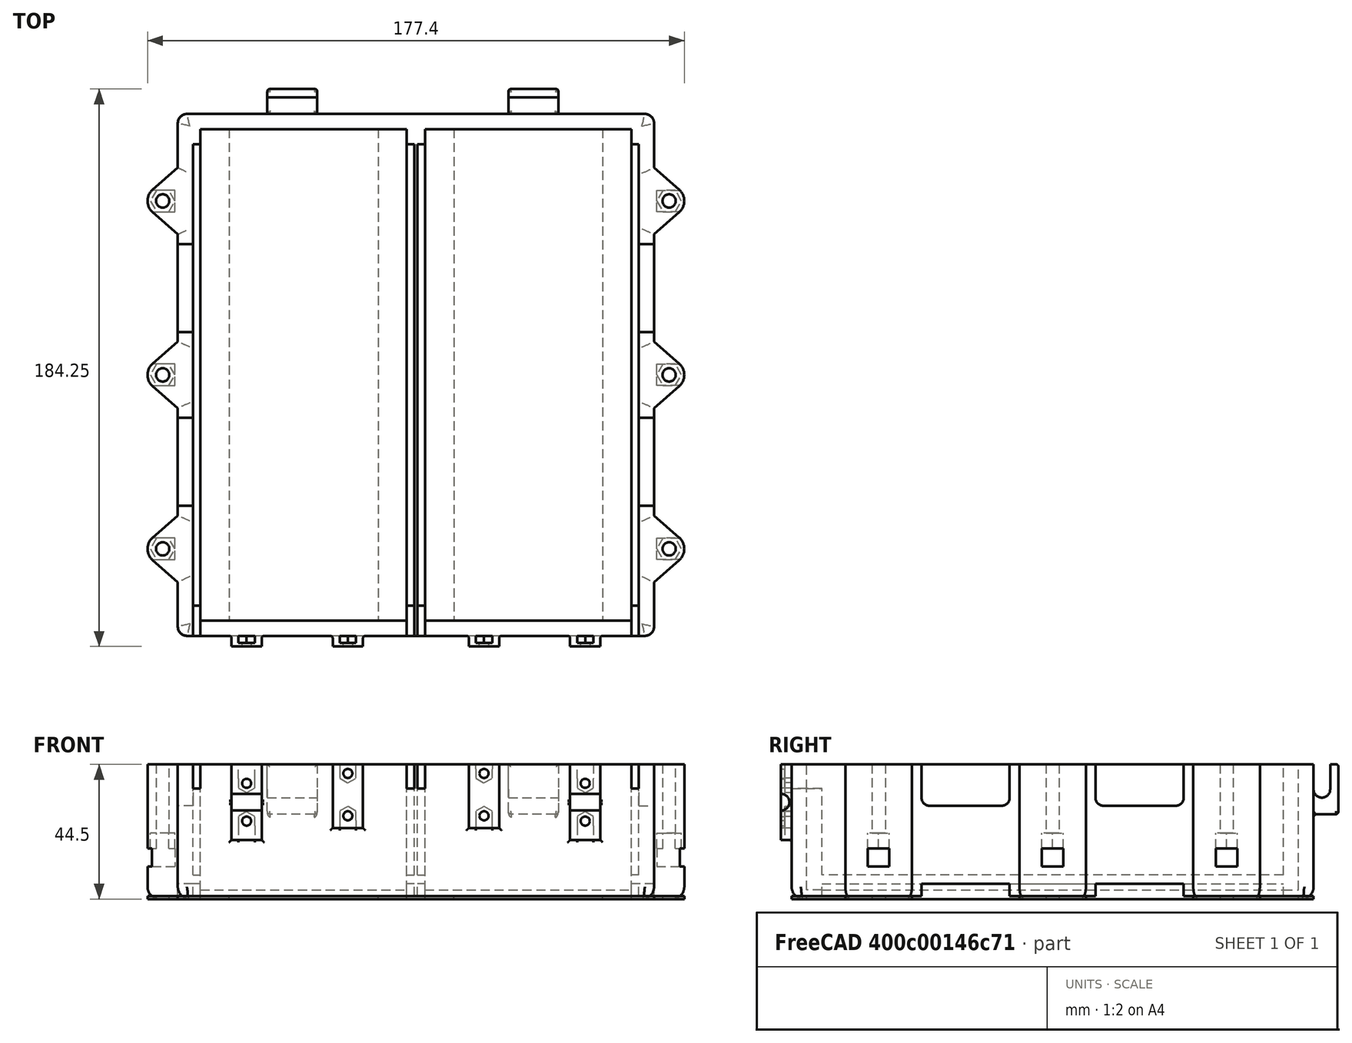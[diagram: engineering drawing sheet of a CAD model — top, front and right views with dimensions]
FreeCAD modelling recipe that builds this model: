
FCSTD DOCUMENT  (FreeCAD 0.19R24291 (Git))
Label: eskate-battery
License: All rights reserved
LicenseURL: http://en.wikipedia.org/wiki/All_rights_reserved
objects: Sketcher::SketchObject×20, PartDesign::Pocket×13, PartDesign::Plane×10, PartDesign::Fillet×10, PartDesign::Pad×7, TechDraw::DrawViewDimension×3, Spreadsheet::Sheet×2, PartDesign::Body×2, TechDraw::DrawViewPart×2, TechDraw::DrawSVGTemplate×1, PartDesign::ShapeBinder×1, TechDraw::DrawPage×1
note: 93 computed .brp shape members not serialized (recipe doc carries the construction recipe); baked Part::Feature solids carry a one-line shape summary decoded from their .brp

FEATURE [Spreadsheet::Sheet] Spreadsheet  label="measurements"
  cells = A1=batteryWidth; B1(batteryWidth)==67.2mm + batteryTolerance; D1=tolerance:; E1(batteryTolerance)==1mm; G1=cableSupportLength; H1(cableSupportLength)==25mm; J1=balanceLeadSlotHeight; K1(balanceLeadSlotHeight)==8mm; A2=batteryHeight; B2(batteryHeight)==40.5mm; G2=cableSupportWidth; H2(cableSupportWidth)=10; A3=batteryLength; B3(batteryLength)==161.5mm + batteryTolerance; D3=todo: add tolerance - but breaks sketch; G3=cableSupportHeight; H3(cableSupportHeight)==3.5mm; I3=cable to fit in 5.5mm radius; G4=cableCompressedRadius; H4(cableCompressedRadius)=2.75; A5=verticalWallThickness; B5(verticalWallThickness)==5mm; G5=m3NutAcrossFlats; H5(m3NutAcrossFlats)=5.4; A6=horizontalWallThickness; B6(horizontalWallThickness)==3mm; G6=m3NutHight; H6(m3NutHight)=2.3; A7=separatorWallThickness; B7(separatorWallThickness)==1mm; G7=m3ScrewHoleRadius; H7(m3ScrewHoleRadius)=1.5; A8=insulatorWallThickness; B8(insulatorWallThickness)==1mm; A10=nickleClearance; B10(nickleClearance)==2.5mm; A11=spacerOverlap; B11(spacerOverlap)==5mm; A13=mountingBumpRadius; B13(mountingBumpRadius)==5mm; A14=boltHoleRadius; B14(boltHoleRadius)=2.2; A15=mountingBumpTangentLength; B15(mountingBumpTangentLength)==11mm; A17=cableRadius; B17(cableRadius)==2.54mm; D17=cableRadiusLarger; E17(cableRadiusLarger)==2.75mm; A18=cableSlotWidth; B18(cableSlotWidth)==24mm; A19=balanceCableRadius; B19(balanceCableRadius)==1.25mm; A21=nutWidth; B21(nutWidth)=7.1; A22=nutHeight; B22(nutHeight)==6mm; A23=nutInsetDepth; B23(nutInsetDepth)==5mm; A25=baseFilletRadius; B25(baseFilletRadius)==4mm; A26=wallFilletRadius; B26(wallFilletRadius)==3mm; A28=spacerHeight; B28(spacerHeight)==9mm; D28=spacerTolerance; E28(spacerTolerance)==0.5mm; A29=spacerKnobbleHeight; B29(spacerKnobbleHeight)==1.6mm; C29=unused; A30=coverThickness; B30(coverThickness)==1mm
FEATURE [Sketcher::SketchObject] Sketch  label="container_shape"
  FullyConstrained = true
  MapMode = 5
  Support = -> [XY_Plane]
  expr: Constraints[23] = .Constraints.boxLength / 3
  expr: Constraints[22] = .Constraints.batteryBoxWidth / 2 + Spreadsheet.mountingBumpRadius
  expr: Constraints[65] = Spreadsheet.mountingBumpTangentLength
  expr: Constraints[19] = .Constraints.batteryBoxWidth / 2 + Spreadsheet.mountingBumpRadius
  expr: Constraints[18] = Spreadsheet.mountingBumpRadius
  expr: .Constraints.boxLength = Spreadsheet.batteryLength + 2 * Spreadsheet.verticalWallThickness
  expr: .Constraints.batteryBoxWidth = 2 * Spreadsheet.batteryWidth + 4 * Spreadsheet.nickleClearance + Spreadsheet.separatorWallThickness + 2 * Spreadsheet.verticalWallThickness
  sketch-geometry (36):
    g0: LineSegment StartX=-78.7 StartY=86.25 StartZ=0 EndX=78.7 EndY=86.25 EndZ=0
    g1: LineSegment StartX=78.7 StartY=86.25 StartZ=0 EndX=78.7 EndY=-86.25 EndZ=0
    g2: LineSegment StartX=78.7 StartY=-86.25 StartZ=0 EndX=-78.7 EndY=-86.25 EndZ=0
    g3: LineSegment StartX=-78.7 StartY=-86.25 StartZ=0 EndX=-78.7 EndY=86.25 EndZ=0
    g4: Circle CenterX=-83.7 CenterY=57.5 CenterZ=0 NormalX=0 NormalY=0 NormalZ=1 AngleXU=0 Radius=5
    g5: Circle CenterX=-83.7 CenterY=0 CenterZ=0 NormalX=0 NormalY=0 NormalZ=1 AngleXU=0 Radius=5
    g6: Circle CenterX=-83.7 CenterY=-57.5 CenterZ=0 NormalX=0 NormalY=0 NormalZ=1 AngleXU=0 Radius=5
    g7: Circle CenterX=83.7 CenterY=-57.5 CenterZ=0 NormalX=0 NormalY=0 NormalZ=1 AngleXU=0 Radius=5
    g8: Circle CenterX=83.7 CenterY=0 CenterZ=0 NormalX=0 NormalY=0 NormalZ=1 AngleXU=0 Radius=5
    g9: Circle CenterX=83.7 CenterY=57.5 CenterZ=0 NormalX=0 NormalY=0 NormalZ=1 AngleXU=0 Radius=5
    g10: LineSegment StartX=86.9877 StartY=61.2671 StartZ=0 EndX=78.7 EndY=68.5 EndZ=0
    g11: LineSegment StartX=86.9877 StartY=53.7329 StartZ=0 EndX=78.7 EndY=46.5 EndZ=0
    g12: LineSegment StartX=86.9877 StartY=3.76712 StartZ=0 EndX=78.7 EndY=11 EndZ=0
    g13: LineSegment StartX=86.9877 StartY=-3.76712 StartZ=0 EndX=78.7 EndY=-11 EndZ=0
    g14: LineSegment StartX=86.9877 StartY=-53.7329 StartZ=0 EndX=78.7 EndY=-46.5 EndZ=0
    g15: LineSegment StartX=86.9877 StartY=-61.2671 StartZ=0 EndX=78.7 EndY=-68.5 EndZ=0
    g16: LineSegment StartX=-86.9877 StartY=-61.2671 StartZ=0 EndX=-78.7 EndY=-68.5 EndZ=0
    g17: LineSegment StartX=-86.9877 StartY=-53.7329 StartZ=0 EndX=-78.7 EndY=-46.5 EndZ=0
    g18: LineSegment StartX=-86.9877 StartY=-3.76713 StartZ=0 EndX=-78.7 EndY=-11 EndZ=0
    g19: LineSegment StartX=-86.9877 StartY=3.76713 StartZ=0 EndX=-78.7 EndY=11 EndZ=0
    g20: LineSegment StartX=-86.9877 StartY=53.7329 StartZ=0 EndX=-78.7 EndY=46.5 EndZ=0
    g21: LineSegment StartX=-86.9877 StartY=61.2671 StartZ=0 EndX=-78.7 EndY=68.5 EndZ=0
    g22: ArcOfCircle CenterX=-83.7 CenterY=57.5 CenterZ=0 NormalX=0 NormalY=0 NormalZ=1 AngleXU=0 Radius=5 StartAngle=2.28834 EndAngle=3.99485
    g23: ArcOfCircle CenterX=-83.7 CenterY=0 CenterZ=0 NormalX=0 NormalY=0 NormalZ=1 AngleXU=0 Radius=5 StartAngle=2.28834 EndAngle=3.99485
    g24: ArcOfCircle CenterX=-83.7 CenterY=-57.5 CenterZ=0 NormalX=0 NormalY=0 NormalZ=1 AngleXU=0 Radius=5 StartAngle=2.28834 EndAngle=3.99485
    g25: ArcOfCircle CenterX=83.7 CenterY=-57.5 CenterZ=0 NormalX=0 NormalY=0 NormalZ=1 AngleXU=0 Radius=5 StartAngle=5.42993 EndAngle=7.13644
    g26: ArcOfCircle CenterX=83.7 CenterY=0 CenterZ=0 NormalX=0 NormalY=0 NormalZ=1 AngleXU=0 Radius=5 StartAngle=5.42993 EndAngle=7.13644
    g27: ArcOfCircle CenterX=83.7 CenterY=57.5 CenterZ=0 NormalX=0 NormalY=0 NormalZ=1 AngleXU=0 Radius=5 StartAngle=5.42993 EndAngle=7.13644
    g28: LineSegment StartX=78.7 StartY=86.25 StartZ=0 EndX=78.7 EndY=68.5 EndZ=0
    g29: LineSegment StartX=78.7 StartY=46.5 StartZ=0 EndX=78.7 EndY=11 EndZ=0
    g30: LineSegment StartX=78.7 StartY=-11 StartZ=0 EndX=78.7 EndY=-46.5 EndZ=0
    g31: LineSegment StartX=78.7 StartY=-68.5 StartZ=0 EndX=78.7 EndY=-86.25 EndZ=0
    g32: LineSegment StartX=-78.7 StartY=-86.25 StartZ=0 EndX=-78.7 EndY=-68.5 EndZ=0
    g33: LineSegment StartX=-78.7 StartY=-46.5 StartZ=0 EndX=-78.7 EndY=-11 EndZ=0
    g34: LineSegment StartX=-78.7 StartY=11 StartZ=0 EndX=-78.7 EndY=46.5 EndZ=0
    g35: LineSegment StartX=-78.7 StartY=68.5 StartZ=0 EndX=-78.7 EndY=86.25 EndZ=0
  constraints (100):
    c: Coincident(g0,g1)
    c: Coincident(g1,g2)
    c: Coincident(g2,g3)
    c: Coincident(g3,g0)
    c: Horizontal(g2)
    c: Vertical(g1)
    c: Symmetric(g0,g2,g-1)
    c: Symmetric(g0,g0,g-2)
    c: DistanceY(g3,g3) = 172.5  'boxLength'
    c: DistanceX(g0,g0) = 157.4  'batteryBoxWidth'
    c: Symmetric(g8,g5,g-2)
    c: Symmetric(g4,g9,g-2)
    c: Symmetric(g6,g7,g-2)
    c: Equal(g4,g9)
    c: Equal(g4,g8)
    c: Equal(g4,g7)
    c: Equal(g4,g5)
    c: Equal(g4,g6)
    c: Radius(g4) = 5
    c: DistanceX(g4,g-1) = 83.7
    c: Symmetric(g4,g6,g-1)
    c: PointOnObject(g5,g-1)
    c: DistanceX(g5,g-1) = 83.7
    c: DistanceY(g-1,g4) = 57.5
    c: PointOnObject(g10,g9)
    c: PointOnObject(g10,g1)
    c: PointOnObject(g11,g1)
    c: Tangent(g11,g9)
    c: PointOnObject(g12,g8)
    c: PointOnObject(g12,g1)
    c: PointOnObject(g13,g1)
    c: PointOnObject(g14,g7)
    c: PointOnObject(g14,g1)
    c: PointOnObject(g15,g1)
    c: PointOnObject(g16,g3)
    c: PointOnObject(g17,g6)
    c: PointOnObject(g17,g3)
    c: PointOnObject(g18,g3)
    c: PointOnObject(g19,g5)
    c: PointOnObject(g19,g3)
    c: PointOnObject(g20,g3)
    c: PointOnObject(g21,g4)
    c: PointOnObject(g21,g3)
    c: Tangent(g21,g4)
    c: Tangent(g20,g4)
    c: Tangent(g19,g5)
    c: Tangent(g5,g18)
    c: Tangent(g17,g6)
    c: Tangent(g6,g16)
    c: Tangent(g15,g7)
    c: Tangent(g7,g14)
    c: Tangent(g13,g8)
    c: Tangent(g12,g8)
    c: Tangent(g10,g9)
    c: Equal(g19,g20)
    c: Equal(g20,g21)
    c: Equal(g21,g18)
    c: Equal(g18,g17)
    c: Equal(g17,g16)
    c: Equal(g16,g15)
    c: Equal(g15,g14)
    c: Equal(g14,g13)
    c: Equal(g13,g12)
    c: Equal(g12,g11)
    c: Equal(g11,g10)
    c: Distance(g21) = 11
    c: Coincident(g22,g21)
    c: Coincident(g22,g20)
    c: Coincident(g22,g4)
    c: Coincident(g23,g5)
    c: Coincident(g23,g19)
    c: Coincident(g23,g18)
    c: Coincident(g24,g6)
    c: Coincident(g24,g17)
    c: Coincident(g24,g16)
    c: Coincident(g25,g7)
    c: Coincident(g25,g15)
    c: Coincident(g25,g14)
    c: Coincident(g26,g8)
    c: Coincident(g26,g12)
    c: Coincident(g26,g13)
    c: Coincident(g27,g9)
    c: Coincident(g27,g11)
    c: Coincident(g27,g10)
    c: Coincident(g28,g0)
    c: Coincident(g28,g10)
    c: Coincident(g29,g11)
    c: Coincident(g30,g13)
    c: Coincident(g31,g15)
    c: Coincident(g32,g2)
    c: Coincident(g33,g17)
    c: Coincident(g34,g19)
    c: Coincident(g35,g21)
    c: Coincident(g29,g12)
    c: Coincident(g30,g14)
    c: Coincident(g31,g2)
    c: Coincident(g32,g16)
    c: Coincident(g33,g18)
    c: Coincident(g34,g20)
    c: Coincident(g35,g0)
FEATURE [PartDesign::Plane] DatumPlane  label="floor_offset"
  AttachmentOffset = pos=(0,0,3) rot=(0,0,1;0rad)
  Length = 213.489
  MapMode = 5
  Placement = pos=(0,0,3) rot=(0,0,1;0rad)
  ResizeMode = 0
  Support = -> [XY_Plane]
  Width = 220.402
  expr: .AttachmentOffset.Base.z = Spreadsheet.horizontalWallThickness
FEATURE [Sketcher::SketchObject] Sketch001  label="battery_space"
  FullyConstrained = true
  MapMode = 5
  Placement = pos=(0,0,3) rot=(0,0,1;0rad)
  Support = -> [DatumPlane]
  expr: Constraints[57] = Spreadsheet.separatorWallThickness
  expr: Constraints[54] = Spreadsheet.nickleClearance
  expr: Constraints[55] = Spreadsheet.batteryWidth
  expr: Constraints[53] = Spreadsheet.batteryLength - 2 * Spreadsheet.spacerOverlap
  expr: Constraints[52] = Spreadsheet.batteryLength
  sketch-geometry (24):
    g0: LineSegment StartX=-0.5 StartY=76.25 StartZ=0 EndX=-0.5 EndY=-76.25 EndZ=0
    g1: LineSegment StartX=-0.5 StartY=-76.25 StartZ=0 EndX=-3 EndY=-76.25 EndZ=0
    g2: LineSegment StartX=-3 StartY=-76.25 StartZ=0 EndX=-3 EndY=-81.25 EndZ=0
    g3: LineSegment StartX=-3 StartY=-81.25 StartZ=0 EndX=-71.2 EndY=-81.25 EndZ=0
    g4: LineSegment StartX=-71.2 StartY=-81.25 StartZ=0 EndX=-71.2 EndY=-76.25 EndZ=0
    g5: LineSegment StartX=-71.2 StartY=-76.25 StartZ=0 EndX=-73.7 EndY=-76.25 EndZ=0
    g6: LineSegment StartX=-73.7 StartY=-76.25 StartZ=0 EndX=-73.7 EndY=76.25 EndZ=0
    g7: LineSegment StartX=-73.7 StartY=76.25 StartZ=0 EndX=-71.2 EndY=76.25 EndZ=0
    g8: LineSegment StartX=-71.2 StartY=76.25 StartZ=0 EndX=-71.2 EndY=81.25 EndZ=0
    g9: LineSegment StartX=-71.2 StartY=81.25 StartZ=0 EndX=-3 EndY=81.25 EndZ=0
    g10: LineSegment StartX=-3 StartY=81.25 StartZ=0 EndX=-3 EndY=76.25 EndZ=0
    g11: LineSegment StartX=-3 StartY=76.25 StartZ=0 EndX=-0.5 EndY=76.25 EndZ=0
    g12: LineSegment StartX=0.5 StartY=76.25 StartZ=0 EndX=0.5 EndY=-76.25 EndZ=0
    g13: LineSegment StartX=0.5 StartY=-76.25 StartZ=0 EndX=3 EndY=-76.25 EndZ=0
    g14: LineSegment StartX=3 StartY=-76.25 StartZ=0 EndX=3 EndY=-81.25 EndZ=0
    g15: LineSegment StartX=3 StartY=-81.25 StartZ=0 EndX=71.2 EndY=-81.25 EndZ=0
    g16: LineSegment StartX=71.2 StartY=-81.25 StartZ=0 EndX=71.2 EndY=-76.25 EndZ=0
    g17: LineSegment StartX=71.2 StartY=-76.25 StartZ=0 EndX=73.7 EndY=-76.25 EndZ=0
    g18: LineSegment StartX=73.7 StartY=-76.25 StartZ=0 EndX=73.7 EndY=76.25 EndZ=0
    g19: LineSegment StartX=73.7 StartY=76.25 StartZ=0 EndX=71.2 EndY=76.25 EndZ=0
    g20: LineSegment StartX=71.2 StartY=76.25 StartZ=0 EndX=71.2 EndY=81.25 EndZ=0
    g21: LineSegment StartX=71.2 StartY=81.25 StartZ=0 EndX=3 EndY=81.25 EndZ=0
    g22: LineSegment StartX=3 StartY=81.25 StartZ=0 EndX=3 EndY=76.25 EndZ=0
    g23: LineSegment StartX=3 StartY=76.25 StartZ=0 EndX=0.5 EndY=76.25 EndZ=0
  constraints (65):
    c: Coincident(g1,g0)
    c: Horizontal(g1)
    c: Coincident(g2,g1)
    c: Vertical(g2)
    c: Coincident(g3,g2)
    c: Coincident(g4,g3)
    c: Vertical(g4)
    c: Coincident(g5,g4)
    c: Horizontal(g5)
    c: Coincident(g6,g5)
    c: Vertical(g6)
    c: Coincident(g7,g6)
    c: Horizontal(g7)
    c: Coincident(g8,g7)
    c: Vertical(g8)
    c: Coincident(g9,g8)
    c: Horizontal(g9)
    c: Coincident(g10,g9)
    c: Vertical(g10)
    c: Coincident(g11,g10)
    c: Coincident(g11,g0)
    c: Horizontal(g11)
    c: Vertical(g12)
    c: Coincident(g13,g12)
    c: Coincident(g14,g13)
    c: Coincident(g15,g14)
    c: Horizontal(g15)
    c: Coincident(g16,g15)
    c: Vertical(g16)
    c: Coincident(g17,g16)
    c: Coincident(g18,g17)
    c: Vertical(g18)
    c: Coincident(g19,g18)
    c: Horizontal(g19)
    c: Coincident(g20,g19)
    c: Vertical(g20)
    c: Coincident(g21,g20)
    c: Horizontal(g21)
    c: Coincident(g22,g21)
    c: Vertical(g22)
    c: Coincident(g23,g22)
    c: Coincident(g23,g12)
    c: Horizontal(g23)
    c: Symmetric(g0,g12,g-2)
    c: Symmetric(g1,g13,g-2)
    c: Horizontal(g3)
    c: Vertical(g14)
    c: Symmetric(g4,g16,g-2)
    c: Symmetric(g5,g17,g-2)
    c: Symmetric(g0,g0,g-1)
    c: Symmetric(g9,g2,g-1)
    c: Symmetric(g7,g4,g-1)
    c: DistanceY(g2,g9) = 162.5
    c: DistanceY(g0,g0) = 152.5
    c: DistanceX(g1,g1) = 2.5
    c: DistanceX(g3,g3) = 68.2
    c: Equal(g1,g5)
    c: DistanceX(g0,g12) = 1
    c: Equal(g0,g6)
    c: Equal(g0,g12)
    c: Equal(g18,g12)
    c: Equal(g16,g2)
    c: Equal(g22,g10)
    c: Equal(g23,g11)
    c: Equal(g19,g7)
FEATURE [PartDesign::Pad] Pad  label="container_shape_pad"
  Direction = (0,0,1)
  Length = 44.5
  Length2 = 100
  Profile = -> Sketch
  Type = 0
  expr: Length = Spreadsheet.horizontalWallThickness + Spreadsheet.batteryHeight + Spreadsheet.insulatorWallThickness
FEATURE [PartDesign::Pocket] Pocket  label="battery_space_pocket"
  BaseFeature = -> Pad
  Length = 5
  Length2 = 100
  Profile = -> Sketch001
  Reversed = true
  Type = 1
FEATURE [Sketcher::SketchObject] Sketch002  label="battery_support_lip"
  ExternalGeometry = -> [Sketch001]
  FullyConstrained = true
  MapMode = 5
  Placement = pos=(0,0,3) rot=(0,0,1;0rad)
  Support = -> [DatumPlane]
  sketch-geometry (16):
    g0: LineSegment StartX=-73.7 StartY=76.25 StartZ=0 EndX=-71.2 EndY=76.25 EndZ=0
    g1: LineSegment StartX=-71.2 StartY=76.25 StartZ=0 EndX=-71.2 EndY=-76.25 EndZ=0
    g2: LineSegment StartX=-71.2 StartY=-76.25 StartZ=0 EndX=-73.7 EndY=-76.25 EndZ=0
    g3: LineSegment StartX=-73.7 StartY=-76.25 StartZ=0 EndX=-73.7 EndY=76.25 EndZ=0
    g4: LineSegment StartX=71.2 StartY=-76.25 StartZ=0 EndX=73.7 EndY=-76.25 EndZ=0
    g5: LineSegment StartX=73.7 StartY=-76.25 StartZ=0 EndX=73.7 EndY=76.25 EndZ=0
    g6: LineSegment StartX=73.7 StartY=76.25 StartZ=0 EndX=71.2 EndY=76.25 EndZ=0
    g7: LineSegment StartX=71.2 StartY=76.25 StartZ=0 EndX=71.2 EndY=-76.25 EndZ=0
    g8: LineSegment StartX=-3 StartY=76.25 StartZ=0 EndX=-0.5 EndY=76.25 EndZ=0
    g9: LineSegment StartX=-0.5 StartY=76.25 StartZ=0 EndX=-0.5 EndY=-76.25 EndZ=0
    g10: LineSegment StartX=-0.5 StartY=-76.25 StartZ=0 EndX=-3 EndY=-76.25 EndZ=0
    g11: LineSegment StartX=-3 StartY=-76.25 StartZ=0 EndX=-3 EndY=76.25 EndZ=0
    g12: LineSegment StartX=0.5 StartY=-76.25 StartZ=0 EndX=3 EndY=-76.25 EndZ=0
    g13: LineSegment StartX=3 StartY=-76.25 StartZ=0 EndX=3 EndY=76.25 EndZ=0
    g14: LineSegment StartX=3 StartY=76.25 StartZ=0 EndX=0.5 EndY=76.25 EndZ=0
    g15: LineSegment StartX=0.5 StartY=76.25 StartZ=0 EndX=0.5 EndY=-76.25 EndZ=0
  constraints (40):
    c: Coincident(g0,g1)
    c: Coincident(g1,g2)
    c: Coincident(g2,g3)
    c: Coincident(g3,g0)
    c: Horizontal(g0)
    c: Horizontal(g2)
    c: Vertical(g1)
    c: Vertical(g3)
    c: Coincident(g0,g-3)
    c: Coincident(g1,g-4)
    c: Coincident(g4,g5)
    c: Coincident(g5,g6)
    c: Coincident(g6,g7)
    c: Coincident(g7,g4)
    c: Horizontal(g4)
    c: Horizontal(g6)
    c: Vertical(g5)
    c: Vertical(g7)
    c: Coincident(g4,g-5)
    c: Coincident(g5,g-6)
    c: Coincident(g8,g9)
    c: Coincident(g9,g10)
    c: Coincident(g10,g11)
    c: Coincident(g11,g8)
    c: Horizontal(g8)
    c: Horizontal(g10)
    c: Vertical(g9)
    c: Vertical(g11)
    c: Coincident(g8,g-7)
    c: Coincident(g9,g-8)
    c: Coincident(g12,g13)
    c: Coincident(g13,g14)
    c: Coincident(g14,g15)
    c: Coincident(g15,g12)
    c: Horizontal(g12)
    c: Horizontal(g14)
    c: Vertical(g13)
    c: Vertical(g15)
    c: Coincident(g12,g-9)
    c: Coincident(g13,g-10)
FEATURE [PartDesign::Pad] Pad001  label="battery_support_lip_pad"
  BaseFeature = -> Pocket
  Direction = (0,0,1)
  Length = 5
  Length2 = 100
  Profile = -> Sketch002
  Type = 0
  expr: Length = Spreadsheet.spacerOverlap
FEATURE [PartDesign::Plane] DatumPlane001  label="inside_wall_right"
  AttachmentOffset = pos=(0,0,73.7) rot=(0,0,1;0rad)
  Length = 206.882
  MapMode = 5
  Placement = pos=(73.7,-1.64e-14,1.64e-14) rot=(0.57735,0.57735,0.57735;2.0944rad)
  ResizeMode = 0
  Support = -> [YZ_Plane]
  Width = 92.1322
  expr: .AttachmentOffset.Base.z = Spreadsheet.batteryWidth + 2 * Spreadsheet.nickleClearance + 0.5 * Spreadsheet.separatorWallThickness
FEATURE [Sketcher::SketchObject] Sketch003  label="cable_slots_right"
  FullyConstrained = true
  MapMode = 5
  Placement = pos=(73.7,-1.64e-14,1.64e-14) rot=(0.57735,0.57735,0.57735;2.0944rad)
  Support = -> [DatumPlane001]
  expr: Constraints[36] = Spreadsheet.batteryHeight / 2
  expr: Constraints[17] = 1 / 6 * (Spreadsheet.batteryLength + 2 * Spreadsheet.verticalWallThickness) - Spreadsheet.cableSlotWidth / 2
  expr: Constraints[16] = Spreadsheet.cableSlotWidth
  expr: Constraints[15] = 2 * Spreadsheet.cableRadius
  expr: Constraints[14] = 3 / 4 * Spreadsheet.batteryHeight + Spreadsheet.horizontalWallThickness
  sketch-geometry (20):
    g0: ArcOfCircle CenterX=-40.75 CenterY=33.375 CenterZ=0 NormalX=0 NormalY=0 NormalZ=1 AngleXU=0 Radius=2.54 StartAngle=1.5708 EndAngle=4.71239
    g1: ArcOfCircle CenterX=-16.75 CenterY=33.375 CenterZ=0 NormalX=0 NormalY=0 NormalZ=1 AngleXU=0 Radius=2.54 StartAngle=4.71239 EndAngle=7.85398
    g2: LineSegment StartX=-40.75 StartY=30.835 StartZ=0 EndX=-16.75 EndY=30.835 EndZ=0
    g3: LineSegment StartX=-40.75 StartY=35.915 StartZ=0 EndX=-16.75 EndY=35.915 EndZ=0
    g4: ArcOfCircle CenterX=16.75 CenterY=33.375 CenterZ=0 NormalX=0 NormalY=0 NormalZ=1 AngleXU=0 Radius=2.54 StartAngle=1.5708 EndAngle=4.71239
    g5: ArcOfCircle CenterX=40.75 CenterY=33.375 CenterZ=0 NormalX=0 NormalY=0 NormalZ=1 AngleXU=0 Radius=2.54 StartAngle=4.71239 EndAngle=7.85398
    g6: LineSegment StartX=16.75 StartY=30.835 StartZ=0 EndX=40.75 EndY=30.835 EndZ=0
    g7: LineSegment StartX=16.75 StartY=35.915 StartZ=0 EndX=40.75 EndY=35.915 EndZ=0
    g8: LineSegment StartX=43.29 StartY=33.375 StartZ=0 EndX=14.21 EndY=33.375 EndZ=0
    g9: LineSegment StartX=14.21 StartY=33.375 StartZ=0 EndX=14.21 EndY=53.625 EndZ=0
    g10: LineSegment StartX=14.21 StartY=53.625 StartZ=0 EndX=43.29 EndY=53.625 EndZ=0
    g11: LineSegment StartX=43.29 StartY=53.625 StartZ=0 EndX=43.29 EndY=33.375 EndZ=0
    g12: LineSegment StartX=-14.21 StartY=53.625 StartZ=0 EndX=-43.29 EndY=53.625 EndZ=0
    g13: LineSegment StartX=-14.21 StartY=33.375 StartZ=0 EndX=-14.21 EndY=53.625 EndZ=0
    g14: LineSegment StartX=-43.29 StartY=53.625 StartZ=0 EndX=-43.29 EndY=33.375 EndZ=0
    g15: LineSegment StartX=-43.29 StartY=33.375 StartZ=0 EndX=-14.21 EndY=33.375 EndZ=0
    g16: ArcOfCircle CenterX=40.75 CenterY=33.375 CenterZ=0 NormalX=0 NormalY=0 NormalZ=1 AngleXU=0 Radius=2.54 StartAngle=4.71239 EndAngle=6.28319
    g17: ArcOfCircle CenterX=16.75 CenterY=33.375 CenterZ=0 NormalX=0 NormalY=0 NormalZ=1 AngleXU=0 Radius=2.54 StartAngle=3.14159 EndAngle=4.71239
    g18: ArcOfCircle CenterX=-40.75 CenterY=33.375 CenterZ=0 NormalX=0 NormalY=0 NormalZ=1 AngleXU=0 Radius=2.54 StartAngle=3.14159 EndAngle=4.71239
    g19: ArcOfCircle CenterX=-16.75 CenterY=33.375 CenterZ=0 NormalX=0 NormalY=0 NormalZ=1 AngleXU=0 Radius=2.54 StartAngle=4.71239 EndAngle=6.28319
  constraints (49):
    c: Tangent(g0,g3) = 1.5708
    c: Tangent(g0,g2) = -1.5708
    c: Tangent(g2,g1) = -1.5708
    c: Tangent(g3,g1) = 1.5708
    c: Horizontal(g2)
    c: Equal(g0,g1)
    c: Tangent(g4,g7) = 1.5708
    c: Tangent(g4,g6) = -1.5708
    c: Tangent(g6,g5) = -1.5708
    c: Tangent(g7,g5) = 1.5708
    c: Horizontal(g6)
    c: Symmetric(g4,g1,g-2)
    c: Symmetric(g5,g0,g-2)
    c: Horizontal(g7)
    c: DistanceY(g-1,g1) = 33.375
    c: DistanceY(g1,g1) = 5.08
    c: DistanceX(g0,g1) = 24
    c: DistanceX(g1,g-1) = 16.75
    c: Coincident(g8,g9)
    c: Coincident(g9,g10)
    c: Coincident(g10,g11)
    c: Coincident(g11,g8)
    c: Horizontal(g8)
    c: Horizontal(g10)
    c: Vertical(g9)
    c: Vertical(g11)
    c: PointOnObject(g4,g8)
    c: Coincident(g15,g13)
    c: Coincident(g13,g12)
    c: Coincident(g12,g14)
    c: Coincident(g14,g15)
    c: Horizontal(g15)
    c: Horizontal(g12)
    c: Vertical(g14)
    c: PointOnObject(g1,g15)
    c: Symmetric(g9,g12,g-2)
    c: DistanceY(g11,g11) = 20.25
    c: Coincident(g16,g5)
    c: Coincident(g16,g6)
    c: Coincident(g16,g11)
    c: Coincident(g17,g4)
    c: Coincident(g17,g9)
    c: Coincident(g17,g6)
    c: Coincident(g18,g0)
    c: Coincident(g18,g2)
    c: Coincident(g18,g14)
    c: Coincident(g19,g1)
    c: Coincident(g19,g13)
    c: Coincident(g19,g2)
FEATURE [PartDesign::Pocket] Pocket001  label="cable_slots_right_pocket"
  BaseFeature = -> Pad001
  Length = 5
  Length2 = 100
  Profile = -> Sketch003
  Reversed = true
  Type = 1
FEATURE [PartDesign::Plane] DatumPlane002  label="inside_wall_left"
  AttachmentOffset = pos=(0,0,-73.7) rot=(0,0,1;0rad)
  Length = 206.882
  MapMode = 5
  Placement = pos=(-73.7,1.64e-14,-1.64e-14) rot=(0.57735,0.57735,0.57735;2.0944rad)
  ResizeMode = 0
  Support = -> [YZ_Plane]
  Width = 92.1322
  expr: .AttachmentOffset.Base.z = -(Spreadsheet.batteryWidth + 2 * Spreadsheet.nickleClearance + 0.5 * Spreadsheet.separatorWallThickness)
FEATURE [Sketcher::SketchObject] Sketch004  label="cable_slots_left"
  ExternalGeometry = -> [Sketch003]
  FullyConstrained = true
  MapMode = 5
  Placement = pos=(-73.7,1.64e-14,-1.64e-14) rot=(0.57735,0.57735,0.57735;2.0944rad)
  Support = -> [DatumPlane002]
  sketch-geometry (12):
    g0: ArcOfCircle CenterX=-40.75 CenterY=33.375 CenterZ=0 NormalX=0 NormalY=0 NormalZ=1 AngleXU=0 Radius=2.54 StartAngle=3.14159 EndAngle=4.71239
    g1: ArcOfCircle CenterX=-16.75 CenterY=33.375 CenterZ=0 NormalX=0 NormalY=0 NormalZ=1 AngleXU=0 Radius=2.54 StartAngle=4.71239 EndAngle=6.28319
    g2: ArcOfCircle CenterX=16.75 CenterY=33.375 CenterZ=0 NormalX=0 NormalY=0 NormalZ=1 AngleXU=0 Radius=2.54 StartAngle=3.14159 EndAngle=4.71239
    g3: ArcOfCircle CenterX=40.75 CenterY=33.375 CenterZ=0 NormalX=0 NormalY=0 NormalZ=1 AngleXU=0 Radius=2.54 StartAngle=4.71239 EndAngle=6.28319
    g4: LineSegment StartX=-40.75 StartY=30.835 StartZ=0 EndX=-16.75 EndY=30.835 EndZ=0
    g5: LineSegment StartX=16.75 StartY=30.835 StartZ=0 EndX=40.75 EndY=30.835 EndZ=0
    g6: LineSegment StartX=-43.29 StartY=53.625 StartZ=0 EndX=-14.21 EndY=53.625 EndZ=0
    g7: LineSegment StartX=14.21 StartY=53.625 StartZ=0 EndX=43.29 EndY=53.625 EndZ=0
    g8: LineSegment StartX=14.21 StartY=53.625 StartZ=0 EndX=14.21 EndY=33.375 EndZ=0
    g9: LineSegment StartX=43.29 StartY=53.625 StartZ=0 EndX=43.29 EndY=33.375 EndZ=0
    g10: LineSegment StartX=-14.21 StartY=53.625 StartZ=0 EndX=-14.21 EndY=33.375 EndZ=0
    g11: LineSegment StartX=-43.29 StartY=53.625 StartZ=0 EndX=-43.29 EndY=33.375 EndZ=0
  constraints (28):
    c: Coincident(g6,g11)
    c: Coincident(g6,g10)
    c: Coincident(g10,g1)
    c: Coincident(g1,g4)
    c: Coincident(g4,g0)
    c: Coincident(g11,g0)
    c: Coincident(g7,g8)
    c: Coincident(g9,g7)
    c: Coincident(g3,g9)
    c: Coincident(g3,g5)
    c: Coincident(g5,g2)
    c: Coincident(g8,g2)
    c: Coincident(g6,g-6)
    c: Coincident(g6,g-6)
    c: DistanceY(g-8,g0) = 0
    c: Coincident(g0,g-8)
    c: Coincident(g0,g-8)
    c: DistanceY(g1,g-7) = 0
    c: Coincident(g1,g-7)
    c: Coincident(g1,g-7)
    c: Coincident(g7,g-5)
    c: Coincident(g7,g-5)
    c: DistanceY(g2,g-3) = 0
    c: DistanceY(g-4,g3) = 0
    c: Coincident(g-4,g3)
    c: Coincident(g-3,g2)
    c: Coincident(g2,g-3)
    c: Coincident(g3,g-4)
FEATURE [PartDesign::Pocket] Pocket002  label="cable_slots_left_pocket"
  BaseFeature = -> Pocket001
  Length = 5
  Length2 = 100
  Profile = -> Sketch004
  Type = 1
FEATURE [PartDesign::Plane] DatumPlane003  label="nut_plane"
  AttachmentOffset = pos=(0,0,16.75) rot=(0,0,1;0rad)
  Length = 213.489
  MapMode = 5
  Placement = pos=(0,0,16.75) rot=(0,0,1;0rad)
  ResizeMode = 0
  Support = -> [XY_Plane]
  Width = 220.402
  expr: .AttachmentOffset.Base.z = (Spreadsheet.batteryHeight + Spreadsheet.horizontalWallThickness) / 2 - Spreadsheet.nutInsetDepth
FEATURE [Sketcher::SketchObject] Sketch005  label="nut_inset"
  ExternalGeometry = -> [Sketch]
  FullyConstrained = true
  MapMode = 5
  Placement = pos=(0,0,16.75) rot=(0,0,1;0rad)
  Support = -> [DatumPlane003]
  expr: Constraints[113] = Spreadsheet.nutWidth
  expr: Constraints[112] = Spreadsheet.nutWidth
  expr: Constraints[111] = Spreadsheet.nutWidth
  expr: Constraints[110] = Spreadsheet.nutWidth
  expr: Constraints[109] = Spreadsheet.nutWidth
  expr: Constraints[108] = Spreadsheet.nutWidth
  sketch-geometry (42):
    g0: LineSegment StartX=-79.6008 StartY=57.5 StartZ=0 EndX=-81.6504 EndY=61.05 EndZ=0
    g1: LineSegment StartX=-81.6504 StartY=61.05 StartZ=0 EndX=-85.7496 EndY=61.05 EndZ=0
    g2: LineSegment StartX=-85.7496 StartY=61.05 StartZ=0 EndX=-87.7992 EndY=57.5 EndZ=0
    g3: LineSegment StartX=-87.7992 StartY=57.5 StartZ=0 EndX=-85.7496 EndY=53.95 EndZ=0
    g4: LineSegment StartX=-85.7496 StartY=53.95 StartZ=0 EndX=-81.6504 EndY=53.95 EndZ=0
    g5: LineSegment StartX=-81.6504 StartY=53.95 StartZ=0 EndX=-79.6008 EndY=57.5 EndZ=0
    g6: Circle CenterX=-83.7 CenterY=57.5 CenterZ=0 NormalX=0 NormalY=0 NormalZ=1 AngleXU=0 Radius=4.09919
    g7: LineSegment StartX=-79.6008 StartY=0 StartZ=0 EndX=-81.6504 EndY=3.55 EndZ=0
    g8: LineSegment StartX=-81.6504 StartY=3.55 StartZ=0 EndX=-85.7496 EndY=3.55 EndZ=0
    g9: LineSegment StartX=-85.7496 StartY=3.55 StartZ=0 EndX=-87.7992 EndY=4e-16 EndZ=0
    g10: LineSegment StartX=-87.7992 StartY=4e-16 StartZ=0 EndX=-85.7496 EndY=-3.55 EndZ=0
    g11: LineSegment StartX=-85.7496 StartY=-3.55 StartZ=0 EndX=-81.6504 EndY=-3.55 EndZ=0
    g12: LineSegment StartX=-81.6504 StartY=-3.55 StartZ=0 EndX=-79.6008 EndY=0 EndZ=0
    g13: Circle CenterX=-83.7 CenterY=0 CenterZ=0 NormalX=0 NormalY=0 NormalZ=1 AngleXU=0 Radius=4.09919
    g14: LineSegment StartX=-81.6504 StartY=-61.05 StartZ=0 EndX=-79.6008 EndY=-57.5 EndZ=0
    g15: LineSegment StartX=-79.6008 StartY=-57.5 StartZ=0 EndX=-81.6504 EndY=-53.95 EndZ=0
    g16: LineSegment StartX=-81.6504 StartY=-53.95 StartZ=0 EndX=-85.7496 EndY=-53.95 EndZ=0
    g17: LineSegment StartX=-85.7496 StartY=-53.95 StartZ=0 EndX=-87.7992 EndY=-57.5 EndZ=0
    g18: LineSegment StartX=-87.7992 StartY=-57.5 StartZ=0 EndX=-85.7496 EndY=-61.05 EndZ=0
    g19: LineSegment StartX=-85.7496 StartY=-61.05 StartZ=0 EndX=-81.6504 EndY=-61.05 EndZ=0
    g20: Circle CenterX=-83.7 CenterY=-57.5 CenterZ=0 NormalX=0 NormalY=0 NormalZ=1 AngleXU=0 Radius=4.09919
    g21: LineSegment StartX=79.6008 StartY=-57.5 StartZ=0 EndX=81.6504 EndY=-61.05 EndZ=0
    g22: LineSegment StartX=81.6504 StartY=-61.05 StartZ=0 EndX=85.7496 EndY=-61.05 EndZ=0
    g23: LineSegment StartX=85.7496 StartY=-61.05 StartZ=0 EndX=87.7992 EndY=-57.5 EndZ=0
    g24: LineSegment StartX=87.7992 StartY=-57.5 StartZ=0 EndX=85.7496 EndY=-53.95 EndZ=0
    g25: LineSegment StartX=85.7496 StartY=-53.95 StartZ=0 EndX=81.6504 EndY=-53.95 EndZ=0
    g26: LineSegment StartX=81.6504 StartY=-53.95 StartZ=0 EndX=79.6008 EndY=-57.5 EndZ=0
    g27: Circle CenterX=83.7 CenterY=-57.5 CenterZ=0 NormalX=0 NormalY=0 NormalZ=1 AngleXU=0 Radius=4.09919
    g28: LineSegment StartX=79.6008 StartY=4e-16 StartZ=0 EndX=81.6504 EndY=-3.55 EndZ=0
    g29: LineSegment StartX=81.6504 StartY=-3.55 StartZ=0 EndX=85.7496 EndY=-3.55 EndZ=0
    g30: LineSegment StartX=85.7496 StartY=-3.55 StartZ=0 EndX=87.7992 EndY=0 EndZ=0
    g31: LineSegment StartX=87.7992 StartY=0 StartZ=0 EndX=85.7496 EndY=3.55 EndZ=0
    g32: LineSegment StartX=85.7496 StartY=3.55 StartZ=0 EndX=81.6504 EndY=3.55 EndZ=0
    g33: LineSegment StartX=81.6504 StartY=3.55 StartZ=0 EndX=79.6008 EndY=4e-16 EndZ=0
    g34: Circle CenterX=83.7 CenterY=0 CenterZ=0 NormalX=0 NormalY=0 NormalZ=1 AngleXU=0 Radius=4.09919
    g35: LineSegment StartX=79.6008 StartY=57.5 StartZ=0 EndX=81.6504 EndY=53.95 EndZ=0
    g36: LineSegment StartX=81.6504 StartY=53.95 StartZ=0 EndX=85.7496 EndY=53.95 EndZ=0
    g37: LineSegment StartX=85.7496 StartY=53.95 StartZ=0 EndX=87.7992 EndY=57.5 EndZ=0
    g38: LineSegment StartX=87.7992 StartY=57.5 StartZ=0 EndX=85.7496 EndY=61.05 EndZ=0
    g39: LineSegment StartX=85.7496 StartY=61.05 StartZ=0 EndX=81.6504 EndY=61.05 EndZ=0
    g40: LineSegment StartX=81.6504 StartY=61.05 StartZ=0 EndX=79.6008 EndY=57.5 EndZ=0
    g41: Circle CenterX=83.7 CenterY=57.5 CenterZ=0 NormalX=0 NormalY=0 NormalZ=1 AngleXU=0 Radius=4.09919
  constraints (96):
    c: Coincident(g0,g1)
    c: Coincident(g1,g2)
    c: Coincident(g2,g3)
    c: Coincident(g3,g4)
    c: Coincident(g4,g5)
    c: Coincident(g5,g0)
    c: Equal(g0, g1-g5) x5
    c: PointOnObject(g0,g6)
    c: PointOnObject(g1,g6)
    c: PointOnObject(g2,g6)
    c: PointOnObject(g3,g6)
    c: PointOnObject(g4,g6)
    c: PointOnObject(g5,g6)
    c: Coincident(g7,g8)
    c: Coincident(g8,g9)
    c: Coincident(g9,g10)
    c: Coincident(g10,g11)
    c: Coincident(g11,g12)
    c: Coincident(g12,g7)
    c: Equal(g7, g8-g12) x5
    c: PointOnObject(g7,g13)
    c: PointOnObject(g8,g13)
    c: PointOnObject(g9,g13)
    c: PointOnObject(g10,g13)
    c: PointOnObject(g11,g13)
    c: PointOnObject(g12,g13)
    c: Coincident(g14,g15)
    c: Coincident(g15,g16)
    c: Coincident(g16,g17)
    c: Coincident(g17,g18)
    c: Coincident(g18,g19)
    c: Coincident(g19,g14)
    c: Equal(g14, g15-g19) x5
    c: PointOnObject(g14,g20)
    c: PointOnObject(g15,g20)
    c: PointOnObject(g16,g20)
    c: PointOnObject(g17,g20)
    c: PointOnObject(g18,g20)
    c: PointOnObject(g19,g20)
    c: Coincident(g21,g22)
    c: Coincident(g22,g23)
    c: Coincident(g23,g24)
    c: Coincident(g24,g25)
    c: Coincident(g25,g26)
    c: Coincident(g26,g21)
    c: Equal(g21, g22-g26) x5
    c: PointOnObject(g21,g27)
    c: PointOnObject(g22,g27)
    c: PointOnObject(g23,g27)
    c: PointOnObject(g24,g27)
    c: PointOnObject(g25,g27)
    c: PointOnObject(g26,g27)
    c: Coincident(g28,g29)
    c: Coincident(g29,g30)
    c: Coincident(g30,g31)
    c: Coincident(g31,g32)
    c: Coincident(g32,g33)
    c: Coincident(g33,g28)
    c: Equal(g28, g29-g33) x5
    c: PointOnObject(g28,g34)
    c: PointOnObject(g29,g34)
    c: PointOnObject(g30,g34)
    c: PointOnObject(g31,g34)
    c: PointOnObject(g32,g34)
    c: PointOnObject(g33,g34)
    c: Coincident(g35,g36)
    c: Coincident(g36,g37)
    c: Coincident(g37,g38)
    c: Coincident(g38,g39)
    c: Coincident(g39,g40)
    c: Coincident(g40,g35)
    c: Equal(g35, g36-g40) x5
    c: PointOnObject(g35,g41)
    c: PointOnObject(g36,g41)
    c: PointOnObject(g37,g41)
    c: PointOnObject(g38,g41)
    c: PointOnObject(g39,g41)
    c: PointOnObject(g40,g41)
    c: Horizontal(g4)
    c: Horizontal(g11)
    c: Horizontal(g19)
    c: Horizontal(g22)
    c: Horizontal(g29)
    c: Horizontal(g36)
    c: DistanceY(g3,g1) = 7.1
    c: DistanceY(g10,g8) = 7.1
    c: DistanceY(g18,g16) = 7.1
    c: DistanceY(g22,g24) = 7.1
    c: DistanceY(g29,g31) = 7.1
    c: DistanceY(g36,g38) = 7.1
    c: Coincident(g6,g-3)
    c: Coincident(g13,g-4)
    c: Coincident(g20,g-5)
    c: Coincident(g27,g-6)
    c: Coincident(g-7,g34)
    c: Coincident(g41,g-8)
FEATURE [Sketcher::SketchObject] Sketch006  label="nut_slot"
  ExternalGeometry = -> [Sketch005]
  FullyConstrained = true
  MapMode = 5
  Placement = pos=(0,0,16.75) rot=(0,0,1;0rad)
  Support = -> [DatumPlane003]
  expr: Constraints[59] = Spreadsheet.mountingBumpRadius * 2
  sketch-geometry (24):
    g0: LineSegment StartX=-79.6008 StartY=61.05 StartZ=0 EndX=-89.6008 EndY=61.05 EndZ=0
    g1: LineSegment StartX=-89.6008 StartY=61.05 StartZ=0 EndX=-89.6008 EndY=53.95 EndZ=0
    g2: LineSegment StartX=-89.6008 StartY=53.95 StartZ=0 EndX=-79.6008 EndY=53.95 EndZ=0
    g3: LineSegment StartX=-79.6008 StartY=53.95 StartZ=0 EndX=-79.6008 EndY=61.05 EndZ=0
    g4: LineSegment StartX=-79.6008 StartY=3.55 StartZ=0 EndX=-89.6008 EndY=3.55 EndZ=0
    g5: LineSegment StartX=-89.6008 StartY=3.55 StartZ=0 EndX=-89.6008 EndY=-3.55 EndZ=0
    g6: LineSegment StartX=-89.6008 StartY=-3.55 StartZ=0 EndX=-79.6008 EndY=-3.55 EndZ=0
    g7: LineSegment StartX=-79.6008 StartY=-3.55 StartZ=0 EndX=-79.6008 EndY=3.55 EndZ=0
    g8: LineSegment StartX=-79.6008 StartY=-53.95 StartZ=0 EndX=-89.6008 EndY=-53.95 EndZ=0
    g9: LineSegment StartX=-89.6008 StartY=-53.95 StartZ=0 EndX=-89.6008 EndY=-61.05 EndZ=0
    g10: LineSegment StartX=-89.6008 StartY=-61.05 StartZ=0 EndX=-79.6008 EndY=-61.05 EndZ=0
    g11: LineSegment StartX=-79.6008 StartY=-61.05 StartZ=0 EndX=-79.6008 EndY=-53.95 EndZ=0
    g12: LineSegment StartX=79.6008 StartY=-53.95 StartZ=0 EndX=89.6008 EndY=-53.95 EndZ=0
    g13: LineSegment StartX=89.6008 StartY=-53.95 StartZ=0 EndX=89.6008 EndY=-61.05 EndZ=0
    g14: LineSegment StartX=89.6008 StartY=-61.05 StartZ=0 EndX=79.6008 EndY=-61.05 EndZ=0
    g15: LineSegment StartX=79.6008 StartY=-61.05 StartZ=0 EndX=79.6008 EndY=-53.95 EndZ=0
    g16: LineSegment StartX=79.6008 StartY=3.55 StartZ=0 EndX=89.6008 EndY=3.55 EndZ=0
    g17: LineSegment StartX=89.6008 StartY=3.55 StartZ=0 EndX=89.6008 EndY=-3.55 EndZ=0
    g18: LineSegment StartX=89.6008 StartY=-3.55 StartZ=0 EndX=79.6008 EndY=-3.55 EndZ=0
    g19: LineSegment StartX=79.6008 StartY=-3.55 StartZ=0 EndX=79.6008 EndY=3.55 EndZ=0
    g20: LineSegment StartX=79.6008 StartY=61.05 StartZ=0 EndX=89.6008 EndY=61.05 EndZ=0
    g21: LineSegment StartX=89.6008 StartY=61.05 StartZ=0 EndX=89.6008 EndY=53.95 EndZ=0
    g22: LineSegment StartX=89.6008 StartY=53.95 StartZ=0 EndX=79.6008 EndY=53.95 EndZ=0
    g23: LineSegment StartX=79.6008 StartY=53.95 StartZ=0 EndX=79.6008 EndY=61.05 EndZ=0
  constraints (60):
    c: Coincident(g0,g1)
    c: Coincident(g1,g2)
    c: Coincident(g2,g3)
    c: Coincident(g3,g0)
    c: Vertical(g1)
    c: Vertical(g3)
    c: Coincident(g4,g5)
    c: Coincident(g5,g6)
    c: Coincident(g6,g7)
    c: Coincident(g7,g4)
    c: Vertical(g5)
    c: Vertical(g7)
    c: Coincident(g8,g9)
    c: Coincident(g9,g10)
    c: Coincident(g10,g11)
    c: Coincident(g11,g8)
    c: Vertical(g9)
    c: Vertical(g11)
    c: Coincident(g12,g13)
    c: Coincident(g13,g14)
    c: Coincident(g14,g15)
    c: Coincident(g15,g12)
    c: Vertical(g13)
    c: Vertical(g15)
    c: Coincident(g16,g17)
    c: Coincident(g17,g18)
    c: Coincident(g18,g19)
    c: Coincident(g19,g16)
    c: Vertical(g17)
    c: Vertical(g19)
    c: Coincident(g20,g21)
    c: Coincident(g21,g22)
    c: Coincident(g22,g23)
    c: Coincident(g23,g20)
    c: Vertical(g21)
    c: Vertical(g23)
    c: PointOnObject(g-5,g3)
    c: PointOnObject(g-8,g7)
    c: PointOnObject(g-11,g11)
    c: PointOnObject(g-14,g15)
    c: PointOnObject(g-17,g19)
    c: PointOnObject(g-20,g23)
    c: Tangent(g0,g-3)
    c: Tangent(g2,g-4)
    c: Tangent(g20,g-18)
    c: Tangent(g-19,g22)
    c: Tangent(g16,g-15)
    c: Tangent(g18,g-16)
    c: Tangent(g12,g-12)
    c: Tangent(g-13,g14)
    c: Tangent(g8,g-9)
    c: Tangent(g10,g-10)
    c: Tangent(g6,g-7)
    c: Tangent(g4,g-6)
    c: Equal(g0,g4)
    c: Equal(g0,g8)
    c: Equal(g0,g20)
    c: Equal(g0,g16)
    c: Equal(g0,g12)
    c: DistanceX(g0,g0) = 10
FEATURE [PartDesign::Pocket] Pocket003  label="nut_slot_pocket"
  BaseFeature = -> Pocket002
  Length = 6
  Length2 = 100
  Profile = -> Sketch006
  Type = 0
  expr: Length = Spreadsheet.nutHeight
FEATURE [PartDesign::Pocket] Pocket004  label="nut_inset_pocket"
  BaseFeature = -> Pocket003
  Length = 5
  Length2 = 100
  Profile = -> Sketch005
  Reversed = true
  Type = 0
  expr: Length = Spreadsheet.nutInsetDepth
FEATURE [Sketcher::SketchObject] Sketch007  label="bolt_holes"
  ExternalGeometry = -> [Sketch]
  FullyConstrained = true
  MapMode = 5
  Placement = pos=(0,0,16.75) rot=(0,0,1;0rad)
  Support = -> [DatumPlane003]
  expr: Constraints[9] = Spreadsheet.boltHoleRadius
  expr: Constraints[8] = Spreadsheet.boltHoleRadius
  expr: Constraints[7] = Spreadsheet.boltHoleRadius
  expr: Constraints[6] = Spreadsheet.boltHoleRadius
  expr: Constraints[11] = Spreadsheet.boltHoleRadius
  expr: Constraints[10] = Spreadsheet.boltHoleRadius
  sketch-geometry (6):
    g0: Circle CenterX=-83.7 CenterY=57.5 CenterZ=0 NormalX=0 NormalY=0 NormalZ=1 AngleXU=0 Radius=2.2
    g1: Circle CenterX=-83.7 CenterY=0 CenterZ=0 NormalX=0 NormalY=0 NormalZ=1 AngleXU=0 Radius=2.2
    g2: Circle CenterX=-83.7 CenterY=-57.5 CenterZ=0 NormalX=0 NormalY=0 NormalZ=1 AngleXU=0 Radius=2.2
    g3: Circle CenterX=83.7 CenterY=-57.5 CenterZ=0 NormalX=0 NormalY=0 NormalZ=1 AngleXU=0 Radius=2.2
    g4: Circle CenterX=83.7 CenterY=0 CenterZ=0 NormalX=0 NormalY=0 NormalZ=1 AngleXU=0 Radius=2.2
    g5: Circle CenterX=83.7 CenterY=57.5 CenterZ=0 NormalX=0 NormalY=0 NormalZ=1 AngleXU=0 Radius=2.2
  constraints (12):
    c: Coincident(g0,g-8)
    c: Coincident(g1,g-5)
    c: Coincident(g2,g-4)
    c: Coincident(g3,g-3)
    c: Coincident(g4,g-6)
    c: Coincident(g5,g-7)
    c: Radius(g5) = 2.2
    c: Radius(g4) = 2.2
    c: Radius(g3) = 2.2
    c: Radius(g2) = 2.2
    c: Radius(g1) = 2.2
    c: Radius(g0) = 2.2
FEATURE [PartDesign::Pocket] Pocket005  label="bolt_holes_pocket"
  BaseFeature = -> Pocket004
  Length = 5
  Length2 = 100
  Profile = -> Sketch007
  Reversed = true
  Type = 1
FEATURE [PartDesign::Fillet] Fillet  label="base_fillet"
  Base = -> Pocket005 [Face4]
  BaseFeature = -> Pocket005
  Radius = 4
  SupportTransform = false
  expr: Radius = Spreadsheet.baseFilletRadius
FEATURE [PartDesign::Fillet] Fillet001  label="wall_corners_fillet"
  Base = -> Fillet [Edge249,Edge124,Edge245,Edge70]
  BaseFeature = -> Fillet
  Radius = 3
  SupportTransform = false
  expr: Radius = Spreadsheet.wallFilletRadius
FEATURE [PartDesign::Plane] DatumPlane004  label="balance_lead_datum_plane"
  AttachmentOffset = pos=(0,0,-76.25) rot=(0,0,1;0rad)
  Length = 199.54
  MapMode = 5
  Placement = pos=(0,76.25,1.69e-14) rot=(1,0,0;1.5708rad)
  ResizeMode = 0
  Support = -> [XZ_Plane]
  Width = 91.7035
  expr: .AttachmentOffset.Base.z = -(Spreadsheet.batteryLength / 2 - Spreadsheet.spacerOverlap)
FEATURE [TechDraw::DrawSVGTemplate] Template
  EditableTexts = Designed_by_Name=Designed by Name; Drawing_number=Drawing number; FC-Date=Date; FC-SC=Scale; FC-SH=Sheet; FC-Title=Title; Subtitle=Subtitle; Weight=Weight
  Height = 210
  Orientation = 1
  Width = 297
FEATURE [PartDesign::ShapeBinder] ShapeBinder
  TraceSupport = false
FEATURE [Sketcher::SketchObject] Sketch010  label="cover_outline"
  ExternalGeometry = -> [ShapeBinder]
  FullyConstrained = false
  MapMode = 5
  Support = -> [XY_Plane001]
  sketch-geometry (32):
    g0: LineSegment StartX=-75.7 StartY=86.25 StartZ=0 EndX=75.7 EndY=86.25 EndZ=0
    g1: LineSegment StartX=-78.7 StartY=83.25 StartZ=0 EndX=-78.7 EndY=68.5 EndZ=0
    g2: LineSegment StartX=-78.7 StartY=46.5 StartZ=0 EndX=-78.7 EndY=11 EndZ=0
    g3: LineSegment StartX=-78.7 StartY=-11 StartZ=0 EndX=-78.7 EndY=-46.5 EndZ=0
    g4: LineSegment StartX=-78.7 StartY=-68.5 StartZ=0 EndX=-78.7 EndY=-83.25 EndZ=0
    g5: LineSegment StartX=-75.7 StartY=-86.25 StartZ=0 EndX=75.7 EndY=-86.25 EndZ=0
    g6: LineSegment StartX=78.7 StartY=-83.25 StartZ=0 EndX=78.7 EndY=-68.5 EndZ=0
    g7: LineSegment StartX=78.7 StartY=-46.5 StartZ=0 EndX=78.7 EndY=-11 EndZ=0
    g8: LineSegment StartX=78.7 StartY=11 StartZ=0 EndX=78.7 EndY=46.5 EndZ=0
    g9: LineSegment StartX=78.7 StartY=68.5 StartZ=0 EndX=78.7 EndY=83.25 EndZ=0
    g10: LineSegment StartX=-78.7 StartY=68.5 StartZ=0 EndX=-86.9877 EndY=61.2671 EndZ=0
    g11: LineSegment StartX=-86.9877 StartY=53.7329 StartZ=0 EndX=-78.7 EndY=46.5 EndZ=0
    g12: LineSegment StartX=-78.7 StartY=11 StartZ=0 EndX=-86.9877 EndY=3.76713 EndZ=0
    g13: LineSegment StartX=-86.9877 StartY=-3.76713 StartZ=0 EndX=-78.7 EndY=-11 EndZ=0
    g14: LineSegment StartX=-78.7 StartY=-46.5 StartZ=0 EndX=-86.9877 EndY=-53.7329 EndZ=0
    g15: LineSegment StartX=-86.9877 StartY=-61.2671 StartZ=0 EndX=-78.7 EndY=-68.5 EndZ=0
    g16: LineSegment StartX=78.7 StartY=-68.5 StartZ=0 EndX=86.9877 EndY=-61.2671 EndZ=0
    g17: LineSegment StartX=86.9877 StartY=-53.7329 StartZ=0 EndX=78.7 EndY=-46.5 EndZ=0
    g18: LineSegment StartX=78.7 StartY=-11 StartZ=0 EndX=86.9877 EndY=-3.76712 EndZ=0
    g19: LineSegment StartX=86.9877 StartY=3.76712 StartZ=0 EndX=78.7 EndY=11 EndZ=0
    g20: LineSegment StartX=78.7 StartY=46.5 StartZ=0 EndX=86.9877 EndY=53.7329 EndZ=0
    g21: LineSegment StartX=86.9877 StartY=61.2671 StartZ=0 EndX=78.7 EndY=68.5 EndZ=0
    g22: ArcOfCircle CenterX=-75.7 CenterY=83.25 CenterZ=0 NormalX=0 NormalY=0 NormalZ=1 AngleXU=0 Radius=3 StartAngle=1.5708 EndAngle=3.14159
    g23: ArcOfCircle CenterX=-83.7 CenterY=57.5 CenterZ=0 NormalX=0 NormalY=0 NormalZ=1 AngleXU=0 Radius=5 StartAngle=2.28834 EndAngle=3.99485
    g24: ArcOfCircle CenterX=-83.7 CenterY=0 CenterZ=0 NormalX=0 NormalY=0 NormalZ=1 AngleXU=0 Radius=5 StartAngle=2.28834 EndAngle=3.99485
    g25: ArcOfCircle CenterX=-83.7 CenterY=-57.5 CenterZ=0 NormalX=0 NormalY=0 NormalZ=1 AngleXU=0 Radius=5 StartAngle=2.28834 EndAngle=3.99485
    g26: ArcOfCircle CenterX=-75.7 CenterY=-83.25 CenterZ=0 NormalX=0 NormalY=0 NormalZ=1 AngleXU=0 Radius=3 StartAngle=3.14159 EndAngle=4.71239
    g27: ArcOfCircle CenterX=75.7 CenterY=-83.25 CenterZ=0 NormalX=0 NormalY=0 NormalZ=1 AngleXU=0 Radius=3 StartAngle=4.71239 EndAngle=6.28319
    g28: ArcOfCircle CenterX=83.7 CenterY=-57.5 CenterZ=0 NormalX=0 NormalY=0 NormalZ=1 AngleXU=0 Radius=5 StartAngle=5.42993 EndAngle=7.13644
    g29: ArcOfCircle CenterX=83.7 CenterY=0 CenterZ=0 NormalX=0 NormalY=0 NormalZ=1 AngleXU=0 Radius=5 StartAngle=5.42993 EndAngle=7.13644
    g30: ArcOfCircle CenterX=83.7 CenterY=57.5 CenterZ=0 NormalX=0 NormalY=0 NormalZ=1 AngleXU=0 Radius=5 StartAngle=5.42993 EndAngle=7.13644
    g31: ArcOfCircle CenterX=75.7 CenterY=83.25 CenterZ=0 NormalX=0 NormalY=0 NormalZ=1 AngleXU=0 Radius=3 StartAngle=0 EndAngle=1.5708
  constraints (32):
    c: Coincident(g10,g1)
    c: Coincident(g11,g2)
    c: Coincident(g12,g2)
    c: Coincident(g13,g3)
    c: Coincident(g14,g3)
    c: Coincident(g15,g4)
    c: Coincident(g16,g6)
    c: Coincident(g17,g7)
    c: Coincident(g18,g7)
    c: Coincident(g19,g8)
    c: Coincident(g20,g8)
    c: Coincident(g21,g9)
    c: Coincident(g22,g0)
    c: Coincident(g22,g1)
    c: Coincident(g23,g10)
    c: Coincident(g23,g11)
    c: Coincident(g24,g12)
    c: Coincident(g24,g13)
    c: Coincident(g25,g14)
    c: Coincident(g25,g15)
    c: Coincident(g26,g4)
    c: Coincident(g26,g5)
    c: Coincident(g27,g5)
    c: Coincident(g27,g6)
    c: Coincident(g28,g16)
    c: Coincident(g28,g17)
    c: Coincident(g29,g18)
    c: Coincident(g29,g19)
    c: Coincident(g30,g20)
    c: Coincident(g30,g21)
    c: Coincident(g31,g9)
    c: Coincident(g31,g0)
FEATURE [Sketcher::SketchObject] Sketch011  label="cover_cutouts"
  ExternalGeometry = -> [ShapeBinder]
  FullyConstrained = false
  MapMode = 5
  Support = -> [XY_Plane001]
  expr: Constraints[37] = Spreadsheet.spacerHeight + Spreadsheet.spacerTolerance
  expr: Constraints[35] = Spreadsheet.spacerHeight + Spreadsheet.spacerTolerance
  expr: Constraints[33] = Spreadsheet.boltHoleRadius
  expr: Constraints[32] = Spreadsheet.boltHoleRadius
  expr: Constraints[30] = Spreadsheet.boltHoleRadius
  expr: Constraints[36] = Spreadsheet.spacerHeight + Spreadsheet.spacerTolerance
  expr: Constraints[31] = Spreadsheet.boltHoleRadius
  expr: Constraints[34] = Spreadsheet.spacerHeight + Spreadsheet.spacerTolerance
  expr: Constraints[29] = Spreadsheet.boltHoleRadius
  expr: Constraints[28] = Spreadsheet.boltHoleRadius
  sketch-geometry (22):
    g0: Circle CenterX=-83.7 CenterY=57.5 CenterZ=0 NormalX=0 NormalY=0 NormalZ=1 AngleXU=0 Radius=2.2
    g1: Circle CenterX=-83.7 CenterY=0 CenterZ=0 NormalX=0 NormalY=0 NormalZ=1 AngleXU=0 Radius=2.2
    g2: Circle CenterX=-83.7 CenterY=-57.5 CenterZ=0 NormalX=0 NormalY=0 NormalZ=1 AngleXU=0 Radius=2.2
    g3: Circle CenterX=83.7 CenterY=-57.5 CenterZ=0 NormalX=0 NormalY=0 NormalZ=1 AngleXU=0 Radius=2.2
    g4: Circle CenterX=83.7 CenterY=0 CenterZ=0 NormalX=0 NormalY=0 NormalZ=1 AngleXU=0 Radius=2.2
    g5: Circle CenterX=83.7 CenterY=57.5 CenterZ=0 NormalX=0 NormalY=0 NormalZ=1 AngleXU=0 Radius=2.2
    g6: LineSegment StartX=-71.2 StartY=81.25 StartZ=0 EndX=-61.7 EndY=81.25 EndZ=0
    g7: LineSegment StartX=-61.7 StartY=81.25 StartZ=0 EndX=-61.7 EndY=-81.25 EndZ=0
    g8: LineSegment StartX=-61.7 StartY=-81.25 StartZ=0 EndX=-71.2 EndY=-81.25 EndZ=0
    g9: LineSegment StartX=-71.2 StartY=-81.25 StartZ=0 EndX=-71.2 EndY=81.25 EndZ=0
    g10: LineSegment StartX=-3 StartY=81.25 StartZ=0 EndX=-12.5 EndY=81.25 EndZ=0
    g11: LineSegment StartX=-12.5 StartY=81.25 StartZ=0 EndX=-12.5 EndY=-81.25 EndZ=0
    g12: LineSegment StartX=-12.5 StartY=-81.25 StartZ=0 EndX=-3 EndY=-81.25 EndZ=0
    g13: LineSegment StartX=-3 StartY=-81.25 StartZ=0 EndX=-3 EndY=81.25 EndZ=0
    g14: LineSegment StartX=3 StartY=81.25 StartZ=0 EndX=12.5 EndY=81.25 EndZ=0
    g15: LineSegment StartX=12.5 StartY=81.25 StartZ=0 EndX=12.5 EndY=-81.25 EndZ=0
    g16: LineSegment StartX=12.5 StartY=-81.25 StartZ=0 EndX=3 EndY=-81.25 EndZ=0
    g17: LineSegment StartX=3 StartY=-81.25 StartZ=0 EndX=3 EndY=81.25 EndZ=0
    g18: LineSegment StartX=71.2 StartY=81.25 StartZ=0 EndX=61.7 EndY=81.25 EndZ=0
    g19: LineSegment StartX=61.7 StartY=81.25 StartZ=0 EndX=61.7 EndY=-81.25 EndZ=0
    g20: LineSegment StartX=61.7 StartY=-81.25 StartZ=0 EndX=71.2 EndY=-81.25 EndZ=0
    g21: LineSegment StartX=71.2 StartY=-81.25 StartZ=0 EndX=71.2 EndY=81.25 EndZ=0
  constraints (38):
    c: Coincident(g6,g7)
    c: Coincident(g7,g8)
    c: Coincident(g8,g9)
    c: Coincident(g9,g6)
    c: Horizontal(g6)
    c: Horizontal(g8)
    c: Vertical(g7)
    c: Coincident(g10,g11)
    c: Coincident(g11,g12)
    c: Coincident(g12,g13)
    c: Coincident(g13,g10)
    c: Horizontal(g10)
    c: Horizontal(g12)
    c: Vertical(g11)
    c: Coincident(g14,g15)
    c: Coincident(g15,g16)
    c: Coincident(g16,g17)
    c: Coincident(g17,g14)
    c: Horizontal(g14)
    c: Horizontal(g16)
    c: Vertical(g15)
    c: Coincident(g18,g19)
    c: Coincident(g19,g20)
    c: Coincident(g20,g21)
    c: Coincident(g21,g18)
    c: Horizontal(g18)
    c: Horizontal(g20)
    c: Vertical(g19)
    c: Radius(g0) = 2.2
    c: Radius(g1) = 2.2
    c: Radius(g2) = 2.2
    c: Radius(g5) = 2.2
    c: Radius(g4) = 2.2
    c: Radius(g3) = 2.2
    c: Distance(g8) = 9.5
    c: Distance(g12) = 9.5
    c: Distance(g16) = 9.5
    c: Distance(g20) = 9.5
FEATURE [PartDesign::Pad] Pad002  label="cover_outline_pad"
  Direction = (1,1,1)
  Length = 1
  Length2 = 100
  Profile = -> Sketch010
  Type = 0
  expr: Length = Spreadsheet.coverThickness
FEATURE [PartDesign::Pocket] Pocket008  label="cover_cutouts_pocket"
  BaseFeature = -> Pad002
  Length = 5
  Length2 = 100
  Profile = -> Sketch011
  Reversed = true
  Type = 1
FEATURE [PartDesign::Plane] DatumPlane005  label="top_of_cover"
  AttachmentOffset = pos=(0,0,1) rot=(0,0,1;0rad)
  Length = 212.305
  MapMode = 5
  Placement = pos=(0,0,1) rot=(0,0,1;0rad)
  ResizeMode = 0
  Support = -> [XY_Plane001]
  Width = 207.479
  expr: .AttachmentOffset.Base.z = Spreadsheet.coverThickness
FEATURE [Sketcher::SketchObject] Sketch012  label="cover_keying"
  ExternalGeometry = -> [ShapeBinder]
  FullyConstrained = false
  MapMode = 5
  Placement = pos=(0,0,1) rot=(0,0,1;0rad)
  Support = -> [DatumPlane005]
  sketch-geometry (32):
    g0: LineSegment StartX=-73.7 StartY=-76.25 StartZ=0 EndX=-71.2 EndY=-76.25 EndZ=0
    g1: LineSegment StartX=-71.2 StartY=-76.25 StartZ=0 EndX=-71.2 EndY=76.25 EndZ=0
    g2: LineSegment StartX=-71.2 StartY=76.25 StartZ=0 EndX=-73.7 EndY=76.25 EndZ=0
    g3: LineSegment StartX=71.2 StartY=76.25 StartZ=0 EndX=73.7 EndY=76.25 EndZ=0
    g4: LineSegment StartX=73.7 StartY=-76.25 StartZ=0 EndX=71.2 EndY=-76.25 EndZ=0
    g5: LineSegment StartX=71.2 StartY=-76.25 StartZ=0 EndX=71.2 EndY=76.25 EndZ=0
    g6: LineSegment StartX=-3 StartY=-76.25 StartZ=0 EndX=-0.5 EndY=-76.25 EndZ=0
    g7: LineSegment StartX=-0.5 StartY=-76.25 StartZ=0 EndX=-0.5 EndY=76.25 EndZ=0
    g8: LineSegment StartX=-0.5 StartY=76.25 StartZ=0 EndX=-3 EndY=76.25 EndZ=0
    g9: LineSegment StartX=-3 StartY=76.25 StartZ=0 EndX=-3 EndY=-76.25 EndZ=0
    g10: LineSegment StartX=0.5 StartY=76.25 StartZ=0 EndX=3 EndY=76.25 EndZ=0
    g11: LineSegment StartX=3 StartY=76.25 StartZ=0 EndX=3 EndY=-76.25 EndZ=0
    g12: LineSegment StartX=3 StartY=-76.25 StartZ=0 EndX=0.5 EndY=-76.25 EndZ=0
    g13: LineSegment StartX=0.5 StartY=-76.25 StartZ=0 EndX=0.5 EndY=76.25 EndZ=0
    g14: LineSegment StartX=-78.7 StartY=-43.29 StartZ=0 EndX=-73.7 EndY=-43.29 EndZ=0
    g15: LineSegment StartX=-73.7 StartY=-14.21 StartZ=0 EndX=-78.7 EndY=-14.21 EndZ=0
    g16: LineSegment StartX=-78.7 StartY=-14.21 StartZ=0 EndX=-78.7 EndY=-43.29 EndZ=0
    g17: LineSegment StartX=-78.7 StartY=14.21 StartZ=0 EndX=-73.7 EndY=14.21 EndZ=0
    g18: LineSegment StartX=-73.7 StartY=43.29 StartZ=0 EndX=-78.7 EndY=43.29 EndZ=0
    g19: LineSegment StartX=-78.7 StartY=43.29 StartZ=0 EndX=-78.7 EndY=14.21 EndZ=0
    g20: LineSegment StartX=78.7 StartY=14.21 StartZ=0 EndX=73.7 EndY=14.21 EndZ=0
    g21: LineSegment StartX=73.7 StartY=43.29 StartZ=0 EndX=78.7 EndY=43.29 EndZ=0
    g22: LineSegment StartX=78.7 StartY=43.29 StartZ=0 EndX=78.7 EndY=14.21 EndZ=0
    g23: LineSegment StartX=78.7 StartY=-43.29 StartZ=0 EndX=73.7 EndY=-43.29 EndZ=0
    g24: LineSegment StartX=73.7 StartY=-14.21 StartZ=0 EndX=78.7 EndY=-14.21 EndZ=0
    g25: LineSegment StartX=78.7 StartY=-14.21 StartZ=0 EndX=78.7 EndY=-43.29 EndZ=0
    g26: LineSegment StartX=73.7 StartY=43.29 StartZ=0 EndX=73.7 EndY=76.25 EndZ=0
    g27: LineSegment StartX=73.7 StartY=-14.21 StartZ=0 EndX=73.7 EndY=14.21 EndZ=0
    g28: LineSegment StartX=73.7 StartY=-43.29 StartZ=0 EndX=73.7 EndY=-76.25 EndZ=0
    g29: LineSegment StartX=-73.7 StartY=-76.25 StartZ=0 EndX=-73.7 EndY=-43.29 EndZ=0
    g30: LineSegment StartX=-73.7 StartY=-14.21 StartZ=0 EndX=-73.7 EndY=14.21 EndZ=0
    g31: LineSegment StartX=-73.7 StartY=43.29 StartZ=0 EndX=-73.7 EndY=76.25 EndZ=0
  constraints (64):
    c: Coincident(g0,g1)
    c: Coincident(g1,g2)
    c: Horizontal(g0)
    c: Horizontal(g2)
    c: Vertical(g1)
    c: Coincident(g4,g5)
    c: Coincident(g5,g3)
    c: Horizontal(g3)
    c: Horizontal(g4)
    c: Vertical(g5)
    c: Coincident(g6,g7)
    c: Coincident(g7,g8)
    c: Coincident(g8,g9)
    c: Coincident(g9,g6)
    c: Horizontal(g6)
    c: Horizontal(g8)
    c: Vertical(g7)
    c: Vertical(g9)
    c: Coincident(g10,g11)
    c: Coincident(g11,g12)
    c: Coincident(g12,g13)
    c: Coincident(g13,g10)
    c: Horizontal(g10)
    c: Horizontal(g12)
    c: Vertical(g11)
    c: Vertical(g13)
    c: Coincident(g15,g16)
    c: Coincident(g16,g14)
    c: Horizontal(g14)
    c: Horizontal(g15)
    c: Vertical(g16)
    c: Coincident(g18,g19)
    c: Coincident(g19,g17)
    c: Horizontal(g17)
    c: Horizontal(g18)
    c: Vertical(g19)
    c: Coincident(g21,g22)
    c: Coincident(g22,g20)
    c: Horizontal(g20)
    c: Horizontal(g21)
    c: Vertical(g22)
    c: Coincident(g24,g25)
    c: Coincident(g25,g23)
    c: Horizontal(g23)
    c: Horizontal(g24)
    c: Vertical(g25)
    c: Coincident(g26,g21)
    c: Coincident(g26,g3)
    c: Vertical(g26)
    c: Coincident(g27,g24)
    c: Coincident(g27,g20)
    c: Vertical(g27)
    c: Coincident(g28,g23)
    c: Coincident(g28,g4)
    c: Vertical(g28)
    c: Coincident(g29,g0)
    c: Coincident(g29,g14)
    c: Vertical(g29)
    c: Coincident(g30,g15)
    c: Coincident(g30,g17)
    c: Vertical(g30)
    c: Coincident(g31,g18)
    c: Coincident(g31,g2)
    c: Vertical(g31)
FEATURE [PartDesign::Pad] Pad003  label="cover_keying_pad"
  BaseFeature = -> Pocket008
  Direction = (1,1,1)
  Length = 4
  Length2 = 100
  Profile = -> Sketch012
  Type = 0
  expr: Length = Spreadsheet.spacerOverlap - Spreadsheet.coverThickness
FEATURE [PartDesign::Body] Body001  label="cover"
  Group = -> [ShapeBinder,Sketch010,Sketch011,Pad002,Pocket008,Sketch012,DatumPlane005,Pad003]
  Origin = -> Origin001
  Tip = -> Pad003
FEATURE [PartDesign::Plane] DatumPlane006  label="backOuterEdge"
  Length = 199.54
  MapMode = 5
  Placement = pos=(0,-86.25,0) rot=(1,0,0;1.5708rad)
  ResizeMode = 0
  Width = 91.7035
  expr: .Placement.Base.y = -86.25mm
FEATURE [Sketcher::SketchObject] Sketch013  label="backCableSupportShape"
  ExternalGeometry = -> [Pad]
  FullyConstrained = false
  MapMode = 5
  Placement = pos=(0,-86.25,0) rot=(1,0,0;1.5708rad)
  Support = -> [DatumPlane006]
  expr: Constraints[19] = Spreadsheet.horizontalWallThickness + Spreadsheet.batteryHeight + Spreadsheet.insulatorWallThickness - Spreadsheet.cableSupportLength / 2
  expr: Constraints[17] = Spreadsheet.cableSupportWidth
  expr: Constraints[18] = Spreadsheet.cableSupportLength
  expr: Constraints[22] = Spreadsheet.batteryWidth * 2 / 6
  sketch-geometry (10):
    g0: LineSegment StartX=-60.9667 StartY=44.5 StartZ=0 EndX=-50.9667 EndY=44.5 EndZ=0
    g1: LineSegment StartX=-50.9667 StartY=44.5 StartZ=0 EndX=-50.9667 EndY=19.5 EndZ=0
    g2: LineSegment StartX=-50.9667 StartY=19.5 StartZ=0 EndX=-60.9667 EndY=19.5 EndZ=0
    g3: LineSegment StartX=-60.9667 StartY=19.5 StartZ=0 EndX=-60.9667 EndY=44.5 EndZ=0
    g4: LineSegment StartX=50.9667 StartY=44.5 StartZ=0 EndX=60.9667 EndY=44.5 EndZ=0
    g5: LineSegment StartX=60.9667 StartY=44.5 StartZ=0 EndX=60.9667 EndY=19.5 EndZ=0
    g6: LineSegment StartX=60.9667 StartY=19.5 StartZ=0 EndX=50.9667 EndY=19.5 EndZ=0
    g7: LineSegment StartX=50.9667 StartY=19.5 StartZ=0 EndX=50.9667 EndY=44.5 EndZ=0
    g8: LineSegment StartX=-138.149 StartY=32 StartZ=0 EndX=160.98 EndY=32 EndZ=0
    g9: LineSegment StartX=55.9667 StartY=62.7867 StartZ=0 EndX=55.9667 EndY=-29.5025 EndZ=0
  constraints (24):
    c: Coincident(g0,g1)
    c: Coincident(g1,g2)
    c: Coincident(g2,g3)
    c: Coincident(g3,g0)
    c: Horizontal(g0)
    c: Horizontal(g2)
    c: Vertical(g1)
    c: Vertical(g3)
    c: Coincident(g4,g5)
    c: Coincident(g5,g6)
    c: Coincident(g6,g7)
    c: Coincident(g7,g4)
    c: Horizontal(g4)
    c: Vertical(g5)
    c: Vertical(g7)
    c: Symmetric(g1,g6,g-2)
    c: Symmetric(g0,g4,g-2)
    c: Distance(g2) = 10
    c: Distance(g3) = 25
    c: DistanceY(g-1,g8) = 32
    c: Symmetric(g5,g6,g9)
    c: Symmetric(g4,g5,g8)
    c: DistanceX(g9,g-3) = 22.7333
    c: Vertical(g9)
FEATURE [PartDesign::Pad] Pad004  label="backCableSupportShapePad"
  BaseFeature = -> Fillet001
  Direction = (1,1,1)
  Length = 3.5
  Length2 = 100
  Profile = -> Sketch013
  Type = 0
  expr: Length = Spreadsheet.cableSupportHeight
FEATURE [PartDesign::Plane] DatumPlane007  label="cableSupportSidePlane"
  Length = 206.882
  MapMode = 5
  Placement = pos=(0,0,0) rot=(0.57735,0.57735,0.57735;2.0944rad)
  ResizeMode = 0
  Support = -> [YZ_Plane]
  Width = 92.1322
FEATURE [Sketcher::SketchObject] Sketch014  label="cableHoleCutOut"
  ExternalGeometry = -> [Sketch013]
  FullyConstrained = false
  MapMode = 5
  Placement = pos=(0,0,0) rot=(0.57735,0.57735,0.57735;2.0944rad)
  Support = -> [DatumPlane007]
  expr: Constraints[22] = Spreadsheet.batteryHeight + Spreadsheet.horizontalWallThickness + Spreadsheet.insulatorWallThickness
  expr: Constraints[19] = Spreadsheet.cableCompressedRadius
  expr: Constraints[4] = Spreadsheet.batteryLength / 2 + Spreadsheet.verticalWallThickness + Spreadsheet.cableSupportHeight
  expr: Constraints[18] = Spreadsheet.cableCompressedRadius * 3
  expr: Constraints[3] = Spreadsheet.cableCompressedRadius
  sketch-geometry (9):
    g0: ArcOfCircle CenterX=-89.75 CenterY=32 CenterZ=0 NormalX=0 NormalY=0 NormalZ=1 AngleXU=0 Radius=2.75 StartAngle=4.71239 EndAngle=7.85398
    g1: LineSegment StartX=-89.75 StartY=34.75 StartZ=0 EndX=-89.75 EndY=29.25 EndZ=0
    g2: LineSegment StartX=-28.6967 StartY=32 StartZ=0 EndX=40.6711 EndY=32 EndZ=0
    g3: ArcOfCircle CenterX=89 CenterY=36.25 CenterZ=0 NormalX=0 NormalY=0 NormalZ=1 AngleXU=0 Radius=2.75 StartAngle=3.14159 EndAngle=6.28319
    g4: LineSegment StartX=86.25 StartY=36.25 StartZ=0 EndX=86.25 EndY=44.5 EndZ=0
    g5: LineSegment StartX=91.75 StartY=36.25 StartZ=0 EndX=91.75 EndY=44.5 EndZ=0
    g6: LineSegment StartX=91.75 StartY=44.5 StartZ=0 EndX=86.25 EndY=44.5 EndZ=0
    g7: LineSegment StartX=91.75 StartY=36.25 StartZ=0 EndX=86.25 EndY=36.25 EndZ=0
    g8: LineSegment StartX=86.25 StartY=44.5 StartZ=0 EndX=86.25 EndY=14.1243 EndZ=0
  constraints (23):
    c: Coincident(g1,g0)
    c: Coincident(g1,g0)
    c: PointOnObject(g0,g1)
    c: Radius(g0) = 2.75
    c: DistanceX(g0,g-1) = 89.75
    c: Symmetric(g0,g0,g2)
    c: Symmetric(g-3,g-3,g2)
    c: Coincident(g4,g3)
    c: Vertical(g4)
    c: Coincident(g5,g3)
    c: Vertical(g5)
    c: Coincident(g6,g5)
    c: Coincident(g6,g4)
    c: Horizontal(g6)
    c: Coincident(g7,g3)
    c: Coincident(g7,g3)
    c: Horizontal(g7)
    c: PointOnObject(g3,g7)
    c: DistanceY(g3,g4) = 8.25
    c: Radius(g3) = 2.75
    c: Symmetric(g8,g-3,g-2)
    c: Tangent(g4,g8)
    c: DistanceY(g-1,g4) = 44.5
FEATURE [Sketcher::SketchObject] Sketch015  label="m3ScrewHoles"
  ExternalGeometry = -> [Sketch013]
  FullyConstrained = false
  MapMode = 5
  Placement = pos=(0,-86.25,0) rot=(1,0,0;1.5708rad)
  Support = -> [DatumPlane006]
  expr: Constraints[9] = Spreadsheet.m3ScrewHoleRadius
  expr: Constraints[8] = Spreadsheet.m3ScrewHoleRadius
  expr: Constraints[7] = Spreadsheet.m3ScrewHoleRadius
  expr: Constraints[6] = Spreadsheet.m3ScrewHoleRadius
  sketch-geometry (9):
    g0: LineSegment StartX=-55.9667 StartY=48.062 StartZ=0 EndX=-55.9667 EndY=2.30118 EndZ=0
    g1: LineSegment StartX=56.449 StartY=38.25 StartZ=0 EndX=-67.2461 EndY=38.25 EndZ=0
    g2: LineSegment StartX=56.449 StartY=25.75 StartZ=0 EndX=-60.052 EndY=25.75 EndZ=0
    g3: LineSegment StartX=55.9667 StartY=48.062 StartZ=0 EndX=55.9667 EndY=-6.539 EndZ=0
    g4: Circle CenterX=-55.9667 CenterY=38.25 CenterZ=0 NormalX=0 NormalY=0 NormalZ=1 AngleXU=0 Radius=1.5
    g5: Circle CenterX=-55.9667 CenterY=25.75 CenterZ=0 NormalX=0 NormalY=0 NormalZ=1 AngleXU=0 Radius=1.5
    g6: Circle CenterX=55.9667 CenterY=38.25 CenterZ=0 NormalX=0 NormalY=0 NormalZ=1 AngleXU=0 Radius=1.5
    g7: Circle CenterX=55.9667 CenterY=25.75 CenterZ=0 NormalX=0 NormalY=0 NormalZ=1 AngleXU=0 Radius=1.5
    g8: LineSegment StartX=-78.365 StartY=32 StartZ=0 EndX=60.9667 EndY=32 EndZ=0
  constraints (20):
    c: PointOnObject(g4,g0)
    c: PointOnObject(g5,g0)
    c: PointOnObject(g6,g3)
    c: PointOnObject(g7,g3)
    c: PointOnObject(g6,g1)
    c: PointOnObject(g7,g2)
    c: Radius(g6) = 1.5
    c: Radius(g7) = 1.5
    c: Radius(g5) = 1.5
    c: Radius(g4) = 1.5
    c: Symmetric(g-3,g-4,g8)
    c: Symmetric(g1,g2,g8)
    c: Vertical(g0)
    c: Symmetric(g-3,g-3,g3)
    c: Symmetric(g3,g0,g-2)
    c: Horizontal(g2)
    c: Horizontal(g1)
    c: PointOnObject(g5,g2)
    c: PointOnObject(g4,g1)
    c: Symmetric(g-4,g8,g2)
FEATURE [Sketcher::SketchObject] Sketch016  label="cableSupportNutSlots"
  ExternalGeometry = -> [Sketch015]
  FullyConstrained = true
  MapMode = 5
  Placement = pos=(0,-86.25,0) rot=(1,0,0;1.5708rad)
  Support = -> [DatumPlane006]
  expr: Constraints[90] = Spreadsheet.cableSupportLength / 4
  expr: Constraints[89] = Spreadsheet.cableSupportLength / 4
  expr: Constraints[88] = Spreadsheet.cableSupportLength / 4
  expr: Constraints[83] = Spreadsheet.m3NutAcrossFlats
  expr: Constraints[80] = Spreadsheet.m3NutAcrossFlats
  expr: Constraints[87] = Spreadsheet.cableSupportLength / 4
  expr: Constraints[52] = Spreadsheet.m3NutAcrossFlats
  expr: Constraints[78] = Spreadsheet.m3NutAcrossFlats
  expr: Constraints[79] = Spreadsheet.m3NutAcrossFlats
  expr: Constraints[50] = Spreadsheet.m3NutAcrossFlats
  expr: Constraints[51] = Spreadsheet.m3NutAcrossFlats
  expr: Constraints[49] = Spreadsheet.m3NutAcrossFlats
  sketch-geometry (32):
    g0: LineSegment StartX=-53.2667 StartY=36.6912 StartZ=0 EndX=-53.2667 EndY=39.8088 EndZ=0
    g1: LineSegment StartX=-58.6667 StartY=39.8088 StartZ=0 EndX=-58.6667 EndY=36.6912 EndZ=0
    g2: LineSegment StartX=-58.6667 StartY=36.6912 StartZ=0 EndX=-55.9667 EndY=35.1323 EndZ=0
    g3: LineSegment StartX=-55.9667 StartY=35.1323 StartZ=0 EndX=-53.2667 EndY=36.6912 EndZ=0
    g4: Circle CenterX=-55.9667 CenterY=38.25 CenterZ=0 NormalX=0 NormalY=0 NormalZ=1 AngleXU=0 Radius=3.11769
    g5: LineSegment StartX=-53.2667 StartY=24.1912 StartZ=0 EndX=-53.2667 EndY=27.3088 EndZ=0
    g6: LineSegment StartX=-53.2667 StartY=27.3088 StartZ=0 EndX=-55.9667 EndY=28.8677 EndZ=0
    g7: LineSegment StartX=-55.9667 StartY=28.8677 StartZ=0 EndX=-58.6667 EndY=27.3088 EndZ=0
    g8: LineSegment StartX=-58.6667 StartY=27.3088 StartZ=0 EndX=-58.6667 EndY=24.1912 EndZ=0
    g9: Circle CenterX=-55.9667 CenterY=25.75 CenterZ=0 NormalX=0 NormalY=0 NormalZ=1 AngleXU=0 Radius=3.11769
    g10: LineSegment StartX=53.2667 StartY=39.8088 StartZ=0 EndX=53.2667 EndY=36.6912 EndZ=0
    g11: LineSegment StartX=53.2667 StartY=36.6912 StartZ=0 EndX=55.9667 EndY=35.1323 EndZ=0
    g12: LineSegment StartX=55.9667 StartY=35.1323 StartZ=0 EndX=58.6667 EndY=36.6912 EndZ=0
    g13: LineSegment StartX=58.6667 StartY=36.6912 StartZ=0 EndX=58.6667 EndY=39.8088 EndZ=0
    g14: Circle CenterX=55.9667 CenterY=38.25 CenterZ=0 NormalX=0 NormalY=0 NormalZ=1 AngleXU=0 Radius=3.11769
    g15: LineSegment StartX=58.6667 StartY=24.1912 StartZ=0 EndX=58.6667 EndY=27.3088 EndZ=0
    g16: LineSegment StartX=58.6667 StartY=27.3088 StartZ=0 EndX=55.9667 EndY=28.8677 EndZ=0
    g17: LineSegment StartX=55.9667 StartY=28.8677 StartZ=0 EndX=53.2667 EndY=27.3088 EndZ=0
    g18: LineSegment StartX=53.2667 StartY=27.3088 StartZ=0 EndX=53.2667 EndY=24.1912 EndZ=0
    g19: Circle CenterX=55.9667 CenterY=25.75 CenterZ=0 NormalX=0 NormalY=0 NormalZ=1 AngleXU=0 Radius=3.11769
    g20: LineSegment StartX=-58.6667 StartY=39.8088 StartZ=0 EndX=-58.6667 EndY=46.0588 EndZ=0
    g21: LineSegment StartX=-53.2667 StartY=39.8088 StartZ=0 EndX=-53.2667 EndY=46.0588 EndZ=0
    g22: LineSegment StartX=-53.2667 StartY=46.0588 StartZ=0 EndX=-58.6667 EndY=46.0588 EndZ=0
    g23: LineSegment StartX=-58.6667 StartY=24.1912 StartZ=0 EndX=-58.6667 EndY=17.9412 EndZ=0
    g24: LineSegment StartX=-53.2667 StartY=24.1912 StartZ=0 EndX=-53.2667 EndY=17.9412 EndZ=0
    g25: LineSegment StartX=-58.6667 StartY=17.9412 StartZ=0 EndX=-53.2667 EndY=17.9412 EndZ=0
    g26: LineSegment StartX=53.2667 StartY=39.8088 StartZ=0 EndX=53.2667 EndY=46.0588 EndZ=0
    g27: LineSegment StartX=53.2667 StartY=46.0588 StartZ=0 EndX=58.6667 EndY=46.0588 EndZ=0
    g28: LineSegment StartX=58.6667 StartY=46.0588 StartZ=0 EndX=58.6667 EndY=39.8088 EndZ=0
    g29: LineSegment StartX=53.2667 StartY=24.1912 StartZ=0 EndX=53.2667 EndY=17.9412 EndZ=0
    g30: LineSegment StartX=58.6667 StartY=24.1912 StartZ=0 EndX=58.6667 EndY=17.9412 EndZ=0
    g31: LineSegment StartX=58.6667 StartY=17.9412 StartZ=0 EndX=53.2667 EndY=17.9412 EndZ=0
  constraints (92):
    c: Coincident(g1,g2)
    c: Coincident(g2,g3)
    c: Coincident(g3,g0)
    c: Equal(g0,g1)
    c: Equal(g0,g2)
    c: Equal(g0,g3)
    c: PointOnObject(g0,g4)
    c: PointOnObject(g1,g4)
    c: PointOnObject(g1,g4)
    c: PointOnObject(g2,g4)
    c: PointOnObject(g3,g4)
    c: Coincident(g4,g-4)
    c: Coincident(g5,g6)
    c: Coincident(g6,g7)
    c: Coincident(g7,g8)
    c: Equal(g5,g6)
    c: Equal(g5,g7)
    c: Equal(g5,g8)
    c: PointOnObject(g5,g9)
    c: PointOnObject(g6,g9)
    c: PointOnObject(g7,g9)
    c: PointOnObject(g8,g9)
    c: PointOnObject(g5,g9)
    c: Coincident(g9,g-5)
    c: Coincident(g10,g11)
    c: Coincident(g11,g12)
    c: Coincident(g12,g13)
    c: PointOnObject(g10,g14)
    c: PointOnObject(g10,g14)
    c: PointOnObject(g11,g14)
    c: PointOnObject(g12,g14)
    c: PointOnObject(g13,g14)
    c: Coincident(g14,g-3)
    c: Coincident(g15,g16)
    c: Coincident(g16,g17)
    c: Coincident(g17,g18)
    c: Equal(g15,g16)
    c: Equal(g15,g17)
    c: Equal(g15,g18)
    c: PointOnObject(g15,g19)
    c: PointOnObject(g16,g19)
    c: PointOnObject(g17,g19)
    c: PointOnObject(g18,g19)
    c: PointOnObject(g15,g19)
    c: Coincident(g19,g-6)
    c: Vertical(g13)
    c: Vertical(g15)
    c: Vertical(g5)
    c: Vertical(g0)
    c: Distance(g1,g0) = 5.4
    c: Distance(g8,g5) = 5.4
    c: Distance(g18,g15) = 5.4
    c: Distance(g10,g12) = 5.4
    c: Coincident(g21,g0)
    c: Vertical(g21)
    c: Coincident(g22,g21)
    c: Coincident(g22,g20)
    c: Horizontal(g22)
    c: Vertical(g20)
    c: Coincident(g23,g8)
    c: Vertical(g23)
    c: Coincident(g24,g5)
    c: Vertical(g24)
    c: Coincident(g25,g23)
    c: Coincident(g25,g24)
    c: Horizontal(g25)
    c: Vertical(g26)
    c: Coincident(g27,g26)
    c: Coincident(g28,g27)
    c: Vertical(g28)
    c: Horizontal(g27)
    c: Coincident(g29,g18)
    c: Vertical(g29)
    c: Coincident(g30,g15)
    c: Vertical(g30)
    c: Coincident(g31,g30)
    c: Coincident(g31,g29)
    c: Horizontal(g31)
    c: Distance(g1,g0) = 5.4
    c: Distance(g7,g5) = 5.4
    c: Distance(g17,g15) = 5.4
    c: Coincident(g26,g10)
    c: Coincident(g28,g13)
    c: Distance(g10,g13) = 5.4
    c: Equal(g13,g12)
    c: Equal(g12,g11)
    c: Equal(g11,g10)
    c: Distance(g21) = 6.25
    c: Distance(g24) = 6.25
    c: Distance(g28) = 6.25
    c: Distance(g30) = 6.25
    c: Coincident(g1,g20)
FEATURE [PartDesign::Plane] DatumPlane008  label="packOpenSide"
  AttachmentOffset = pos=(0,0,44.5) rot=(0,0,1;0rad)
  Length = 213.489
  MapMode = 5
  Placement = pos=(0,0,44.5) rot=(0,0,1;0rad)
  ResizeMode = 0
  Support = -> [XY_Plane]
  Width = 220.402
  expr: .AttachmentOffset.Base.z = Spreadsheet.batteryHeight + Spreadsheet.horizontalWallThickness + Spreadsheet.insulatorWallThickness
FEATURE [Sketcher::SketchObject] Sketch017  label="balanceCableSlots"
  ExternalGeometry = -> [Sketch001]
  FullyConstrained = true
  MapMode = 5
  Placement = pos=(0,0,44.5) rot=(0,0,1;0rad)
  Support = -> [DatumPlane008]
  expr: Constraints[40] = Spreadsheet.verticalWallThickness * 2
  expr: Constraints[41] = Spreadsheet.verticalWallThickness * 2
  expr: Constraints[42] = Spreadsheet.verticalWallThickness * 2
  expr: Constraints[43] = Spreadsheet.verticalWallThickness * 2
  sketch-geometry (16):
    g0: LineSegment StartX=-73.7 StartY=-76.25 StartZ=0 EndX=-71.2 EndY=-76.25 EndZ=0
    g1: LineSegment StartX=-71.2 StartY=-76.25 StartZ=0 EndX=-71.2 EndY=-86.25 EndZ=0
    g2: LineSegment StartX=-71.2 StartY=-86.25 StartZ=0 EndX=-73.7 EndY=-86.25 EndZ=0
    g3: LineSegment StartX=-73.7 StartY=-86.25 StartZ=0 EndX=-73.7 EndY=-76.25 EndZ=0
    g4: LineSegment StartX=-0.5 StartY=-76.25 StartZ=0 EndX=-3 EndY=-76.25 EndZ=0
    g5: LineSegment StartX=-3 StartY=-76.25 StartZ=0 EndX=-3 EndY=-86.25 EndZ=0
    g6: LineSegment StartX=-3 StartY=-86.25 StartZ=0 EndX=-0.5 EndY=-86.25 EndZ=0
    g7: LineSegment StartX=-0.5 StartY=-86.25 StartZ=0 EndX=-0.5 EndY=-76.25 EndZ=0
    g8: LineSegment StartX=0.5 StartY=-76.25 StartZ=0 EndX=3 EndY=-76.25 EndZ=0
    g9: LineSegment StartX=3 StartY=-76.25 StartZ=0 EndX=3 EndY=-86.25 EndZ=0
    g10: LineSegment StartX=3 StartY=-86.25 StartZ=0 EndX=0.5 EndY=-86.25 EndZ=0
    g11: LineSegment StartX=0.5 StartY=-86.25 StartZ=0 EndX=0.5 EndY=-76.25 EndZ=0
    g12: LineSegment StartX=73.7 StartY=-76.25 StartZ=0 EndX=71.2 EndY=-76.25 EndZ=0
    g13: LineSegment StartX=71.2 StartY=-76.25 StartZ=0 EndX=71.2 EndY=-86.25 EndZ=0
    g14: LineSegment StartX=71.2 StartY=-86.25 StartZ=0 EndX=73.7 EndY=-86.25 EndZ=0
    g15: LineSegment StartX=73.7 StartY=-86.25 StartZ=0 EndX=73.7 EndY=-76.25 EndZ=0
  constraints (44):
    c: Coincident(g0,g1)
    c: Coincident(g1,g2)
    c: Coincident(g2,g3)
    c: Coincident(g3,g0)
    c: Horizontal(g0)
    c: Horizontal(g2)
    c: Vertical(g1)
    c: Vertical(g3)
    c: Coincident(g0,g-3)
    c: Coincident(g4,g5)
    c: Coincident(g5,g6)
    c: Coincident(g6,g7)
    c: Coincident(g7,g4)
    c: Horizontal(g4)
    c: Horizontal(g6)
    c: Vertical(g5)
    c: Vertical(g7)
    c: Coincident(g4,g-4)
    c: Coincident(g8,g9)
    c: Coincident(g9,g10)
    c: Coincident(g10,g11)
    c: Coincident(g11,g8)
    c: Horizontal(g8)
    c: Horizontal(g10)
    c: Vertical(g9)
    c: Vertical(g11)
    c: Coincident(g8,g-5)
    c: Coincident(g12,g13)
    c: Coincident(g13,g14)
    c: Coincident(g14,g15)
    c: Coincident(g15,g12)
    c: Horizontal(g12)
    c: Horizontal(g14)
    c: Vertical(g13)
    c: Vertical(g15)
    c: Coincident(g12,g-6)
    c: PointOnObject(g-8,g13)
    c: PointOnObject(g-8,g9)
    c: PointOnObject(g-7,g5)
    c: PointOnObject(g-7,g1)
    c: Distance(g3) = 10
    c: Distance(g5) = 10
    c: Distance(g9) = 10
    c: Distance(g13) = 10
FEATURE [Sketcher::SketchObject] Sketch018  label="pcbSupportShape"
  FullyConstrained = false
  MapMode = 5
  Placement = pos=(0,-86.25,0) rot=(1,0,0;1.5708rad)
  Support = -> [DatumPlane006]
  expr: Constraints[25] = Spreadsheet.batteryHeight + Spreadsheet.horizontalWallThickness + Spreadsheet.insulatorWallThickness
  expr: Constraints[16] = Spreadsheet001.pcbWidth
  expr: Constraints[18] = Spreadsheet.cableSupportWidth
  expr: Constraints[23] = Spreadsheet001.holeSeparationLength
  sketch-geometry (11):
    g0: LineSegment StartX=-27.5 StartY=44.5 StartZ=0 EndX=-17.5 EndY=44.5 EndZ=0
    g1: LineSegment StartX=-17.5 StartY=44.5 StartZ=0 EndX=-17.5 EndY=23.5 EndZ=0
    g2: LineSegment StartX=-17.5 StartY=23.5 StartZ=0 EndX=-27.5 EndY=23.5 EndZ=0
    g3: LineSegment StartX=-27.5 StartY=23.5 StartZ=0 EndX=-27.5 EndY=44.5 EndZ=0
    g4: LineSegment StartX=17.5 StartY=44.5 StartZ=0 EndX=27.5 EndY=44.5 EndZ=0
    g5: LineSegment StartX=27.5 StartY=44.5 StartZ=0 EndX=27.5 EndY=23.5 EndZ=0
    g6: LineSegment StartX=27.5 StartY=23.5 StartZ=0 EndX=17.5 EndY=23.5 EndZ=0
    g7: LineSegment StartX=17.5 StartY=23.5 StartZ=0 EndX=17.5 EndY=44.5 EndZ=0
    g8: LineSegment StartX=98.7082 StartY=34 StartZ=0 EndX=-116.113 EndY=34 EndZ=0
    g9: LineSegment StartX=-22.5 StartY=62.5682 StartZ=0 EndX=-22.5 EndY=-29.0019 EndZ=0
    g10: LineSegment StartX=22.5 StartY=62.5682 StartZ=0 EndX=22.5 EndY=-29.0019 EndZ=0
  constraints (27):
    c: Coincident(g0,g1)
    c: Coincident(g1,g2)
    c: Coincident(g2,g3)
    c: Coincident(g3,g0)
    c: Horizontal(g0)
    c: Horizontal(g2)
    c: Vertical(g1)
    c: Vertical(g3)
    c: Coincident(g4,g5)
    c: Coincident(g5,g6)
    c: Coincident(g6,g7)
    c: Coincident(g7,g4)
    c: Horizontal(g4)
    c: Horizontal(g6)
    c: Vertical(g7)
    c: Symmetric(g0,g4,g-2)
    c: Distance(g5) = 21
    c: Symmetric(g2,g5,g-2)
    c: Distance(g6) = 10
    c: Symmetric(g4,g5,g8)
    c: Vertical(g9)
    c: Symmetric(g10,g9,g-2)
    c: Equal(g10,g9)
    c: DistanceX(g9,g10) = 45
    c: Symmetric(g4,g4,g10)
    c: DistanceY(g-1,g4) = 44.5
    c: Horizontal(g8)
FEATURE [Spreadsheet::Sheet] Spreadsheet001  label="circuitBoardDimensions"
  cells = A1=pcbWidth; B1(pcbWidth)==21mm; A2=pcbLength; B2(pcbLength)==50mm; A3=holeSeparationWidth; B3(holeSeparationWidth)==14mm; A4=holeSeparationLength; B4(holeSeparationLength)==45mm; A5=bottomHoleFromCentre; B5(bottomHoleFromCentre)==6.5mm
FEATURE [Sketcher::SketchObject] Sketch019  label="pcbBoltHoles"
  ExternalGeometry = -> [Sketch018]
  FullyConstrained = false
  MapMode = 5
  Placement = pos=(0,-86.25,0) rot=(1,0,0;1.5708rad)
  Support = -> [DatumPlane006]
  expr: Constraints[12] = Spreadsheet001.holeSeparationLength
  expr: Constraints[11] = Spreadsheet001.holeSeparationWidth
  expr: Constraints[5] = Spreadsheet.m3ScrewHoleRadius
  expr: Constraints[4] = Spreadsheet.m3ScrewHoleRadius
  expr: Constraints[10] = Spreadsheet001.bottomHoleFromCentre
  expr: Constraints[3] = Spreadsheet.m3ScrewHoleRadius
  expr: Constraints[2] = Spreadsheet.m3ScrewHoleRadius
  sketch-geometry (6):
    g0: Circle CenterX=22.5 CenterY=41.5 CenterZ=0 NormalX=0 NormalY=0 NormalZ=1 AngleXU=0 Radius=1.5
    g1: Circle CenterX=22.5 CenterY=27.5 CenterZ=0 NormalX=0 NormalY=0 NormalZ=1 AngleXU=0 Radius=1.5
    g2: Circle CenterX=-22.5 CenterY=41.5 CenterZ=0 NormalX=0 NormalY=0 NormalZ=1 AngleXU=0 Radius=1.5
    g3: LineSegment StartX=32.0541 StartY=34 StartZ=0 EndX=6.71022 EndY=34 EndZ=0
    g4: Circle CenterX=-22.5 CenterY=27.5 CenterZ=0 NormalX=0 NormalY=0 NormalZ=1 AngleXU=0 Radius=1.5
    g5: LineSegment StartX=22.5 StartY=58.0723 StartZ=0 EndX=22.5 EndY=24.7573 EndZ=0
  constraints (13):
    c: Symmetric(g2,g0,g-2)
    c: Symmetric(g1,g4,g-2)
    c: Radius(g2) = 1.5
    c: Radius(g4) = 1.5
    c: Radius(g0) = 1.5
    c: Radius(g1) = 1.5
    c: Vertical(g5)
    c: PointOnObject(g0,g5)
    c: PointOnObject(g1,g5)
    c: Symmetric(g-3,g-3,g3)
    c: DistanceY(g1,g3) = 6.5
    c: DistanceY(g1,g0) = 14
    c: DistanceX(g4,g1) = 45
FEATURE [Sketcher::SketchObject] Sketch020  label="pcbNutSlots"
  ExternalGeometry = -> [Sketch019,Sketch018]
  FullyConstrained = true
  MapMode = 5
  Placement = pos=(0,-86.25,0) rot=(1,0,0;1.5708rad)
  Support = -> [DatumPlane006]
  expr: Constraints[54] = Spreadsheet.m3NutAcrossFlats
  expr: Constraints[64] = Spreadsheet.m3NutAcrossFlats
  expr: Constraints[65] = Spreadsheet.m3NutAcrossFlats
  expr: Constraints[53] = Spreadsheet.m3NutAcrossFlats
  expr: Constraints[55] = Spreadsheet.m3NutAcrossFlats
  expr: Constraints[52] = Spreadsheet.m3NutAcrossFlats
  expr: Constraints[63] = Spreadsheet.m3NutAcrossFlats
  expr: Constraints[66] = Spreadsheet.m3NutAcrossFlats
  sketch-geometry (32):
    g0: LineSegment StartX=25.2 StartY=39.9412 StartZ=0 EndX=25.2 EndY=43.0588 EndZ=0
    g1: LineSegment StartX=19.8 StartY=43.0588 StartZ=0 EndX=19.8 EndY=39.9412 EndZ=0
    g2: LineSegment StartX=19.8 StartY=39.9412 StartZ=0 EndX=22.5 EndY=38.3823 EndZ=0
    g3: LineSegment StartX=22.5 StartY=38.3823 StartZ=0 EndX=25.2 EndY=39.9412 EndZ=0
    g4: Circle CenterX=22.5 CenterY=41.5 CenterZ=0 NormalX=0 NormalY=0 NormalZ=1 AngleXU=0 Radius=3.11769
    g5: LineSegment StartX=25.2 StartY=25.9412 StartZ=0 EndX=25.2 EndY=29.0588 EndZ=0
    g6: LineSegment StartX=25.2 StartY=29.0588 StartZ=0 EndX=22.5 EndY=30.6177 EndZ=0
    g7: LineSegment StartX=22.5 StartY=30.6177 StartZ=0 EndX=19.8 EndY=29.0588 EndZ=0
    g8: LineSegment StartX=19.8 StartY=29.0588 StartZ=0 EndX=19.8 EndY=25.9412 EndZ=0
    g9: Circle CenterX=22.5 CenterY=27.5 CenterZ=0 NormalX=0 NormalY=0 NormalZ=1 AngleXU=0 Radius=3.11769
    g10: LineSegment StartX=-19.8 StartY=25.9412 StartZ=0 EndX=-19.8 EndY=29.0588 EndZ=0
    g11: LineSegment StartX=-19.8 StartY=29.0588 StartZ=0 EndX=-22.5 EndY=30.6177 EndZ=0
    g12: LineSegment StartX=-22.5 StartY=30.6177 StartZ=0 EndX=-25.2 EndY=29.0588 EndZ=0
    g13: LineSegment StartX=-25.2 StartY=29.0588 StartZ=0 EndX=-25.2 EndY=25.9412 EndZ=0
    g14: Circle CenterX=-22.5 CenterY=27.5 CenterZ=0 NormalX=0 NormalY=0 NormalZ=1 AngleXU=0 Radius=3.11769
    g15: LineSegment StartX=-19.8 StartY=39.9412 StartZ=0 EndX=-19.8 EndY=43.0588 EndZ=0
    g16: LineSegment StartX=-25.2 StartY=43.0588 StartZ=0 EndX=-25.2 EndY=39.9412 EndZ=0
    g17: LineSegment StartX=-25.2 StartY=39.9412 StartZ=0 EndX=-22.5 EndY=38.3823 EndZ=0
    g18: LineSegment StartX=-22.5 StartY=38.3823 StartZ=0 EndX=-19.8 EndY=39.9412 EndZ=0
    g19: Circle CenterX=-22.5 CenterY=41.5 CenterZ=0 NormalX=0 NormalY=0 NormalZ=1 AngleXU=0 Radius=3.11769
    g20: LineSegment StartX=19.8 StartY=43.0588 StartZ=0 EndX=19.8 EndY=44.5 EndZ=0
    g21: LineSegment StartX=19.8 StartY=44.5 StartZ=0 EndX=25.2 EndY=44.5 EndZ=0
    g22: LineSegment StartX=25.2 StartY=44.5 StartZ=0 EndX=25.2 EndY=43.0588 EndZ=0
    g23: LineSegment StartX=19.8 StartY=25.9412 StartZ=0 EndX=19.8 EndY=23.5 EndZ=0
    g24: LineSegment StartX=19.8 StartY=23.5 StartZ=0 EndX=25.2 EndY=23.5 EndZ=0
    g25: LineSegment StartX=25.2 StartY=23.5 StartZ=0 EndX=25.2 EndY=25.9412 EndZ=0
    g26: LineSegment StartX=-25.2 StartY=25.9412 StartZ=0 EndX=-25.2 EndY=23.5 EndZ=0
    g27: LineSegment StartX=-19.8 StartY=25.9412 StartZ=0 EndX=-19.8 EndY=23.5 EndZ=0
    g28: LineSegment StartX=-19.8 StartY=23.5 StartZ=0 EndX=-25.2 EndY=23.5 EndZ=0
    g29: LineSegment StartX=-19.8 StartY=43.0588 StartZ=0 EndX=-19.8 EndY=44.5 EndZ=0
    g30: LineSegment StartX=-19.8 StartY=44.5 StartZ=0 EndX=-25.2 EndY=44.5 EndZ=0
    g31: LineSegment StartX=-25.2 StartY=44.5 StartZ=0 EndX=-25.2 EndY=43.0588 EndZ=0
  constraints (90):
    c: Coincident(g1,g2)
    c: Coincident(g2,g3)
    c: Coincident(g3,g0)
    c: Equal(g0,g1)
    c: Equal(g0,g2)
    c: Equal(g0,g3)
    c: PointOnObject(g0,g4)
    c: PointOnObject(g1,g4)
    c: PointOnObject(g1,g4)
    c: PointOnObject(g2,g4)
    c: PointOnObject(g3,g4)
    c: Coincident(g4,g-3)
    c: Coincident(g5,g6)
    c: Coincident(g6,g7)
    c: Coincident(g7,g8)
    c: Equal(g5,g6)
    c: Equal(g5,g7)
    c: Equal(g5,g8)
    c: PointOnObject(g5,g9)
    c: PointOnObject(g6,g9)
    c: PointOnObject(g7,g9)
    c: PointOnObject(g8,g9)
    c: PointOnObject(g5,g9)
    c: Coincident(g9,g-4)
    c: Coincident(g10,g11)
    c: Coincident(g11,g12)
    c: Coincident(g12,g13)
    c: Equal(g10,g11)
    c: Equal(g10,g12)
    c: Equal(g10,g13)
    c: PointOnObject(g10,g14)
    c: PointOnObject(g11,g14)
    c: PointOnObject(g12,g14)
    c: PointOnObject(g13,g14)
    c: PointOnObject(g10,g14)
    c: Coincident(g14,g-5)
    c: Coincident(g16,g17)
    c: Coincident(g17,g18)
    c: Coincident(g18,g15)
    c: Equal(g15,g16)
    c: Equal(g15,g17)
    c: Equal(g15,g18)
    c: PointOnObject(g15,g19)
    c: PointOnObject(g16,g19)
    c: PointOnObject(g16,g19)
    c: PointOnObject(g17,g19)
    c: PointOnObject(g18,g19)
    c: Coincident(g19,g-6)
    c: Vertical(g16)
    c: Vertical(g1)
    c: Vertical(g8)
    c: Vertical(g13)
    c: DistanceX(g1,g0) = 5.4
    c: DistanceX(g7,g5) = 5.4
    c: DistanceX(g16,g15) = 5.4
    c: DistanceX(g12,g10) = 5.4
    c: Coincident(g20,g1)
    c: Vertical(g20)
    c: Coincident(g21,g20)
    c: Horizontal(g21)
    c: Coincident(g22,g21)
    c: Coincident(g22,g0)
    c: Vertical(g22)
    c: DistanceX(g1,g0) = 5.4
    c: DistanceX(g8,g5) = 5.4
    c: DistanceX(g13,g10) = 5.4
    c: DistanceX(g16,g15) = 5.4
    c: Coincident(g23,g8)
    c: Vertical(g23)
    c: Coincident(g24,g23)
    c: Horizontal(g24)
    c: Coincident(g25,g24)
    c: Coincident(g25,g5)
    c: Coincident(g26,g13)
    c: Vertical(g26)
    c: Coincident(g27,g10)
    c: Vertical(g27)
    c: Coincident(g28,g27)
    c: Coincident(g28,g26)
    c: Coincident(g29,g15)
    c: Vertical(g29)
    c: Coincident(g30,g29)
    c: Horizontal(g30)
    c: Coincident(g31,g30)
    c: Coincident(g31,g16)
    c: Horizontal(g28)
    c: Symmetric(g21,g30,g-2)
    c: Symmetric(g24,g26,g-2)
    c: PointOnObject(g24,g-7)
    c: PointOnObject(g21,g-8)
FEATURE [PartDesign::Plane] DatumPlane009  label="frontOuterEdge"
  AttachmentOffset = pos=(-1,0,-86.25) rot=(0,0,1;0rad)
  Length = 199.54
  MapMode = 5
  Placement = pos=(-1,86.25,1.92e-14) rot=(1,0,0;1.5708rad)
  ResizeMode = 0
  Support = -> [XZ_Plane]
  Width = 91.7035
  expr: .AttachmentOffset.Base.z = -(Spreadsheet.batteryLength / 2 + Spreadsheet.verticalWallThickness)
FEATURE [Sketcher::SketchObject] Sketch021  label="frontCableSupportShape"
  ExternalGeometry = -> [Sketch]
  FullyConstrained = false
  MapMode = 5
  Placement = pos=(-1,86.25,1.92e-14) rot=(1,0,0;1.5708rad)
  Support = -> [DatumPlane009]
  expr: Constraints[23] = Spreadsheet.batteryHeight + Spreadsheet.horizontalWallThickness + Spreadsheet.insulatorWallThickness
  expr: Constraints[18] = Spreadsheet.cableRadiusLarger * 6
  expr: Constraints[17] = Spreadsheet.cableRadiusLarger * 6
  sketch-geometry (11):
    g0: LineSegment StartX=-48.1 StartY=44.5 StartZ=0 EndX=-31.6 EndY=44.5 EndZ=0
    g1: LineSegment StartX=-31.6 StartY=44.5 StartZ=0 EndX=-31.6 EndY=28 EndZ=0
    g2: LineSegment StartX=-31.6 StartY=28 StartZ=0 EndX=-48.1 EndY=28 EndZ=0
    g3: LineSegment StartX=-48.1 StartY=28 StartZ=0 EndX=-48.1 EndY=44.5 EndZ=0
    g4: LineSegment StartX=31.6 StartY=44.5 StartZ=0 EndX=48.1 EndY=44.5 EndZ=0
    g5: LineSegment StartX=48.1 StartY=44.5 StartZ=0 EndX=48.1 EndY=28 EndZ=0
    g6: LineSegment StartX=48.1 StartY=28 StartZ=0 EndX=31.6 EndY=28 EndZ=0
    g7: LineSegment StartX=31.6 StartY=28 StartZ=0 EndX=31.6 EndY=44.5 EndZ=0
    g8: LineSegment StartX=79.7 StartY=52.0073 StartZ=0 EndX=79.7 EndY=7.9214 EndZ=0
    g9: LineSegment StartX=-79.7 StartY=52.0073 StartZ=0 EndX=-79.7 EndY=7.9214 EndZ=0
    g10: LineSegment StartX=39.85 StartY=61.5278 StartZ=0 EndX=39.85 EndY=10.1463 EndZ=0
  constraints (26):
    c: Coincident(g0,g1)
    c: Coincident(g1,g2)
    c: Coincident(g2,g3)
    c: Coincident(g3,g0)
    c: Horizontal(g0)
    c: Horizontal(g2)
    c: Vertical(g1)
    c: Vertical(g3)
    c: Coincident(g4,g5)
    c: Coincident(g5,g6)
    c: Coincident(g6,g7)
    c: Coincident(g7,g4)
    c: Horizontal(g6)
    c: Vertical(g5)
    c: Vertical(g7)
    c: Symmetric(g0,g4,g-2)
    c: Symmetric(g1,g6,g-2)
    c: DistanceX(g0,g0) = 16.5
    c: DistanceY(g3,g3) = 16.5
    c: Vertical(g8)
    c: PointOnObject(g-3,g8)
    c: Symmetric(g8,g9,g-2)
    c: Vertical(g9)
    c: DistanceY(g-1,g4) = 44.5
    c: Symmetric(g-3,g-1,g10)
    c: Symmetric(g4,g4,g10)
FEATURE [PartDesign::Pad] Pad006  label="frontCableSupportShapePad"
  BaseFeature = -> Pad004
  Direction = (1,1,1)
  Length = 8.25
  Length2 = 100
  Profile = -> Sketch021
  Reversed = true
  Type = 0
  expr: Length = Spreadsheet.cableRadiusLarger * 3
FEATURE [PartDesign::Pocket] Pocket009  label="cableHoleCutOutPocket"
  BaseFeature = -> Pad006
  Length = 5
  Length2 = 100
  Midplane = true
  Profile = -> Sketch014
  Type = 1
FEATURE [PartDesign::Pocket] Pocket010  label="m3ScrewHolesPocket"
  BaseFeature = -> Pocket009
  Length = 0
  Length2 = 100
  Profile = -> Sketch015
  Reversed = true
  Type = 1
FEATURE [PartDesign::Pocket] Pocket011  label="cableSupportNutSlotsPocket"
  BaseFeature = -> Pocket010
  Length = 2.3
  Length2 = 100
  Profile = -> Sketch016
  Reversed = true
  Type = 0
  expr: Length = Spreadsheet.m3NutHight
FEATURE [PartDesign::Pocket] Pocket012  label="balanceCableSlotsPocket"
  BaseFeature = -> Pocket011
  Length = 8
  Length2 = 100
  Profile = -> Sketch017
  Type = 0
  expr: Length = Spreadsheet.balanceLeadSlotHeight
FEATURE [PartDesign::Pad] Pad005  label="pcbSupportShapePad"
  BaseFeature = -> Pocket012
  Direction = (1,1,1)
  Length = 3.5
  Length2 = 100
  Profile = -> Sketch018
  Type = 0
  expr: Length = Spreadsheet.cableSupportHeight
FEATURE [PartDesign::Pocket] Pocket013  label="pcbBoltHolesPocket"
  BaseFeature = -> Pad005
  Length = 5
  Length2 = 100
  Profile = -> Sketch019
  Reversed = true
  Type = 1
FEATURE [PartDesign::Pocket] Pocket014  label="pcbNutSlotsPocket"
  BaseFeature = -> Pocket013
  Length = 2.3
  Length2 = 100
  Profile = -> Sketch020
  Reversed = true
  Type = 0
  expr: Length = Spreadsheet.m3NutHight
FEATURE [PartDesign::Fillet] Fillet002
  Base = -> Pocket014 [Face222]
  BaseFeature = -> Pocket014
  Radius = 1
  SupportTransform = false
FEATURE [PartDesign::Fillet] Fillet003
  Base = -> Fillet002 [Face8]
  BaseFeature = -> Fillet002
  Radius = 1
  SupportTransform = false
FEATURE [PartDesign::Fillet] Fillet004
  Base = -> Fillet003 [Face29]
  BaseFeature = -> Fillet003
  Radius = 0.8
  SupportTransform = false
FEATURE [PartDesign::Fillet] Fillet005
  Base = -> Fillet004 [Face33]
  BaseFeature = -> Fillet004
  Radius = 0.8
  SupportTransform = false
FEATURE [PartDesign::Fillet] Fillet006
  Base = -> Fillet005 [Edge232,Edge237,Edge233,Edge238]
  BaseFeature = -> Fillet005
  Radius = 0.8
  SupportTransform = false
FEATURE [PartDesign::Fillet] Fillet007
  Base = -> Fillet006 [Edge47,Edge46,Edge44,Edge43]
  BaseFeature = -> Fillet006
  Radius = 0.8
  SupportTransform = false
FEATURE [PartDesign::Fillet] Fillet008
  Base = -> Fillet007 [Edge39,Edge41,Edge38,Edge42]
  BaseFeature = -> Fillet007
  Radius = 0.8
  SupportTransform = false
FEATURE [PartDesign::Fillet] Fillet009
  Base = -> Fillet008 [Edge5,Edge13,Edge15,Edge3]
  BaseFeature = -> Fillet008
  Radius = 0.8
  SupportTransform = false
FEATURE [PartDesign::Body] Body  label="container"
  Group = -> [Sketch,DatumPlane,Sketch001,Pad,Pocket,Sketch002,Pad001,DatumPlane001,Sketch003,Pocket001,DatumPlane002,Sketch004,Pocket002,DatumPlane003,Sketch005,Sketch006,Pocket003,Pocket004,Sketch007,Pocket005,Fillet,Fillet001,DatumPlane004,DatumPlane006,DatumPlane009,Sketch013,Sketch021,Pad004,Pad006,DatumPlane007,Sketch014,Pocket009,Sketch015,Sketch016,Pocket010,Pocket011,DatumPlane008,Sketch017,Pocket012,+14 more]
  Origin = -> Origin
  Tip = -> Fillet009
FEATURE [TechDraw::DrawViewPart] View  label="Top"
  CoarseView = false
  Direction = (0,0,-1)
  Focus = 100
  HardHidden = false
  IsoCount = 0
  IsoHidden = false
  IsoVisible = false
  LockPosition = false
  Perspective = false
  Rotation = 0
  Scale = 0.5
  ScaleType = 2
  SeamHidden = false
  SeamVisible = true
  SmoothHidden = false
  SmoothVisible = true
  Source = -> [Body]
  X = 66.197
  XDirection = (1,0,0)
  Y = 143.182
FEATURE [TechDraw::DrawViewPart] View001  label="Bottom"
  CoarseView = false
  Direction = (0,0,1)
  Focus = 100
  HardHidden = false
  IsoCount = 0
  IsoHidden = false
  IsoVisible = false
  LockPosition = false
  Perspective = false
  Rotation = 0
  Scale = 0.5
  ScaleType = 2
  SeamHidden = false
  SeamVisible = true
  SmoothHidden = false
  SmoothVisible = true
  Source = -> [Body]
  X = 178.638
  XDirection = (1,0,0)
  Y = 157.517
FEATURE [TechDraw::DrawViewDimension] Dimension002
  Arbitrary = false
  ArbitraryTolerances = false
  EqualTolerance = true
  FormatSpec = %.2w
  FormatSpecOverTolerance = %+.2w
  FormatSpecUnderTolerance = %+.2w
  Inverted = false
  LockPosition = false
  MeasureType = 1
  OverTolerance = 0
  References2D = -> [View001]
  Rotation = 0
  ScaleType = 0
  TheoreticalExact = false
  Type = 1
  UnderTolerance = 0
  X = -46.866
  Y = -57.3616
FEATURE [TechDraw::DrawViewDimension] Dimension
  Arbitrary = false
  ArbitraryTolerances = false
  EqualTolerance = true
  FormatSpec = %.2w
  FormatSpecOverTolerance = %+.2w
  FormatSpecUnderTolerance = %+.2w
  Inverted = false
  LockPosition = false
  MeasureType = 1
  OverTolerance = 0
  References2D = -> [View]
  Rotation = 0
  ScaleType = 0
  TheoreticalExact = false
  Type = 2
  UnderTolerance = 0
  X = 43.5895
  Y = -12.0951
FEATURE [TechDraw::DrawViewDimension] Dimension003
  Arbitrary = false
  ArbitraryTolerances = false
  EqualTolerance = true
  FormatSpec = %.2w
  FormatSpecOverTolerance = %+.2w
  FormatSpecUnderTolerance = %+.2w
  Inverted = false
  LockPosition = false
  MeasureType = 1
  OverTolerance = 0
  References2D = -> [View]
  Rotation = 0
  ScaleType = 0
  TheoreticalExact = false
  Type = 1
  UnderTolerance = 0
  X = 13.9936
  Y = -47.6654
FEATURE [TechDraw::DrawPage] Page
  KeepUpdated = true
  NextBalloonIndex = 1
  ProjectionType = 0
  Template = -> Template
  Views = -> [View,View001,Dimension002,Dimension,Dimension003]
